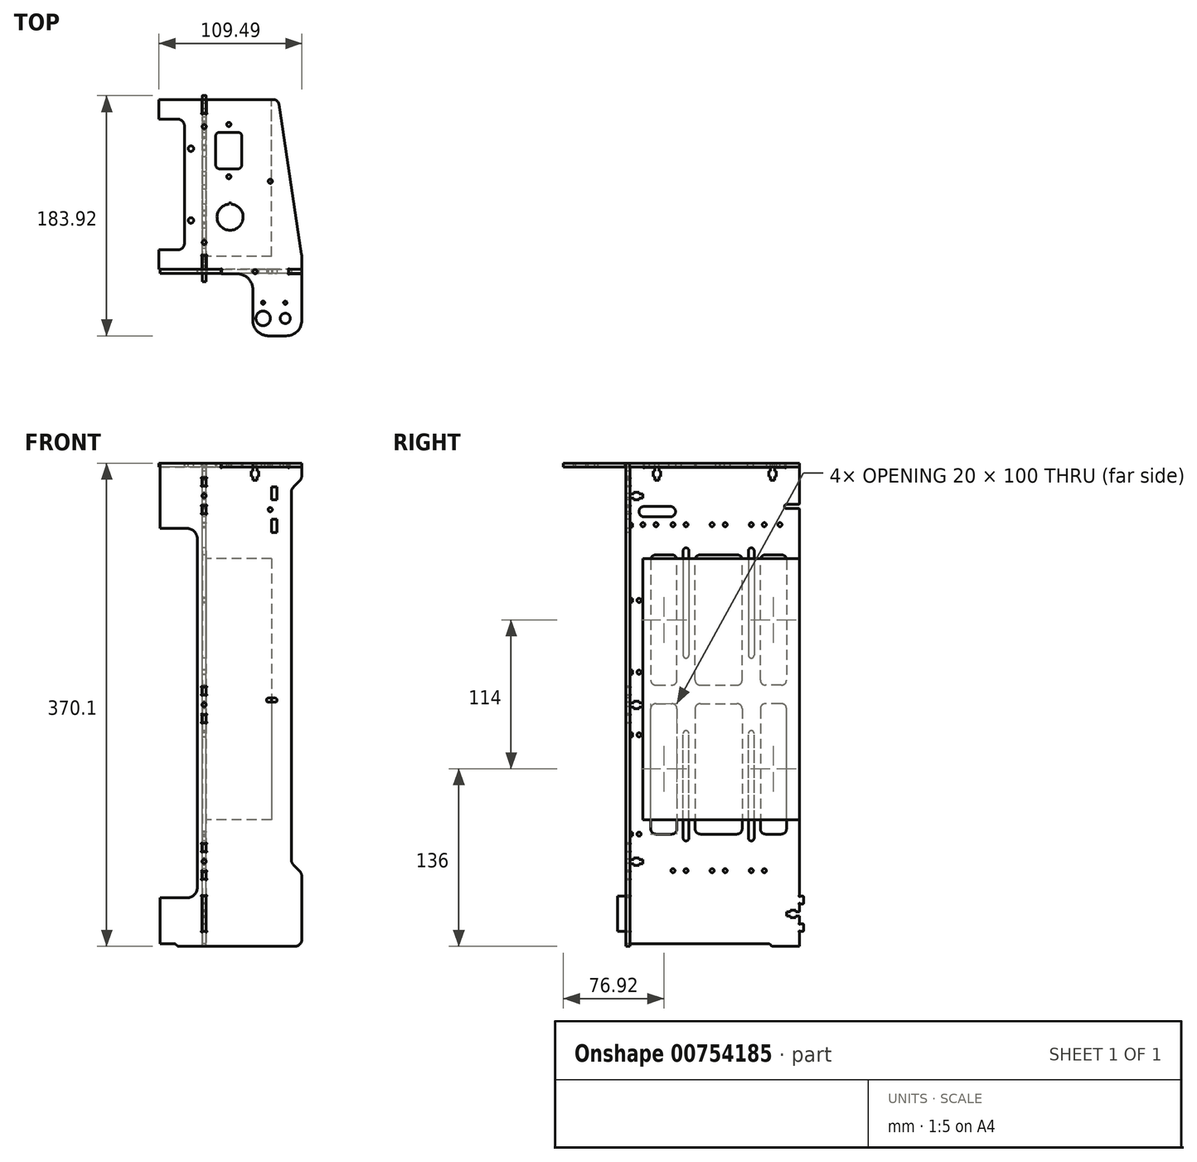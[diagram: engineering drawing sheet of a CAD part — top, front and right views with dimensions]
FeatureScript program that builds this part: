
annotation { "Feature Type Name" : "Feature", "Feature Type Description" : "" }
export const myFeature = defineFeature(function(context is Context, id is Id, definition is map)
    precondition{}
    {
        {
            assignVariable(context, id + "F0", {"name" : "profondeur_alim", "anyValue" : 50});
        }
        {
            var Q0;
            Q0=qCreatedBy(makeId("Top.planeOp"),FACE);
            var sketch = newSketch(context, id + "F1", { "sketchPlane" : qUnion([Q0])});
            skLineSegment(sketch, "E0", {"start": v(194.9, -37.1) * mm, "end": v(185.77, -37.1) * mm});
            skArc(sketch, "E1", {"start": v(185.33, -36.84) * mm, "mid": v(185.52, -37.03) * mm, "end": v(185.77, -37.1) * mm});
            skArc(sketch, "E2", {"start": v(185.33, -36.84) * mm, "mid": v(184.55, -36.74) * mm, "end": v(184.65, -37.53) * mm});
            skArc(sketch, "E3", {"start": v(184.9, -37.96) * mm, "mid": v(184.83, -37.71) * mm, "end": v(184.65, -37.53) * mm});
            skLineSegment(sketch, "E4", {"start": v(184.9, -37.96) * mm, "end": v(184.9, -39.53) * mm});
            skArc(sketch, "E5", {"start": v(184.65, -39.96) * mm, "mid": v(184.83, -39.78) * mm, "end": v(184.9, -39.53) * mm});
            skArc(sketch, "E6", {"start": v(184.65, -39.96) * mm, "mid": v(184.55, -40.75) * mm, "end": v(185.33, -40.64) * mm});
            skArc(sketch, "E7", {"start": v(185.77, -40.4) * mm, "mid": v(185.52, -40.46) * mm, "end": v(185.33, -40.64) * mm});
            skLineSegment(sketch, "E8", {"start": v(185.77, -40.4) * mm, "end": v(194.9, -40.4) * mm});
            skCircle(sketch, "E9", {"center": v(159.08, -38.74) * mm, "radius": 1.6 * mm});
            skLineSegment(sketch, "E10", {"start": v(133.25, -40.4) * mm, "end": v(133.25, -37.92) * mm});
            skArc(sketch, "E11", {"start": v(133.5, -37.48) * mm, "mid": v(133.32, -37.67) * mm, "end": v(133.25, -37.92) * mm});
            skArc(sketch, "E12", {"start": v(133.5, -37.48) * mm, "mid": v(133.6, -36.7) * mm, "end": v(132.82, -36.8) * mm});
            skArc(sketch, "E13", {"start": v(132.38, -37.05) * mm, "mid": v(132.63, -36.98) * mm, "end": v(132.82, -36.8) * mm});
            skLineSegment(sketch, "E14", {"start": v(132.38, -37.05) * mm, "end": v(121.73, -37.05) * mm});
            skLineSegment(sketch, "E15", {"start": v(121.73, -37.05) * mm, "end": v(121.73, -27.27) * mm});
            skArc(sketch, "E16", {"start": v(121.98, -26.83) * mm, "mid": v(121.8, -27.02) * mm, "end": v(121.73, -27.27) * mm});
            skArc(sketch, "E17", {"start": v(121.98, -26.83) * mm, "mid": v(122.08, -26.05) * mm, "end": v(121.3, -26.15) * mm});
            skArc(sketch, "E18", {"start": v(120.86, -26.4) * mm, "mid": v(121.1, -26.33) * mm, "end": v(121.3, -26.15) * mm});
            skLineSegment(sketch, "E19", {"start": v(120.86, -26.4) * mm, "end": v(119.3, -26.4) * mm});
            skArc(sketch, "E20", {"start": v(118.86, -26.15) * mm, "mid": v(119.04, -26.33) * mm, "end": v(119.3, -26.4) * mm});
            skArc(sketch, "E21", {"start": v(118.86, -26.15) * mm, "mid": v(118.07, -26.05) * mm, "end": v(118.18, -26.83) * mm});
            skArc(sketch, "E22", {"start": v(118.43, -27.27) * mm, "mid": v(118.36, -27.02) * mm, "end": v(118.18, -26.83) * mm});
            skLineSegment(sketch, "E23", {"start": v(118.43, -27.27) * mm, "end": v(118.43, -37.05) * mm});
            skCircle(sketch, "E24", {"center": v(120.08, -16.4) * mm, "radius": 1.6 * mm});
            skLineSegment(sketch, "E25", {"start": v(118.43, -37.05) * mm, "end": v(85.41, -37.05) * mm});
            skArc(sketch, "E26", {"start": v(99.9, -22.05) * mm, "mid": v(103.44, -20.58) * mm, "end": v(104.9, -17.05) * mm});
            skLineSegment(sketch, "E27", {"start": v(99.9, -22.05) * mm, "end": v(85.41, -22.05) * mm});
            skCircle(sketch, "E28", {"center": v(109.9, 0.45) * mm, "radius": 2.1 * mm});
            skLineSegment(sketch, "E29", {"start": v(194.9, -40.4) * mm, "end": v(194.9, -75.92) * mm});
            skArc(sketch, "E30", {"start": v(182.9, -87.92) * mm, "mid": v(191.39, -84.4) * mm, "end": v(194.9, -75.92) * mm});
            skCircle(sketch, "E31", {"center": v(182.2, -62.54) * mm, "radius": 1.25 * mm});
            skCircle(sketch, "E32", {"center": v(165.2, -74.55) * mm, "radius": 5.53 * mm});
            skCircle(sketch, "E33", {"center": v(165.2, -62.54) * mm, "radius": 1.25 * mm});
            skCircle(sketch, "E34", {"center": v(182.2, -74.54) * mm, "radius": 3.9 * mm});
            skLineSegment(sketch, "E35", {"start": v(194.9, -37.1) * mm, "end": v(194.9, -28.66) * mm});
            skArc(sketch, "E36", {"start": v(194.9, -28.66) * mm, "mid": v(194.84, -27.1) * mm, "end": v(194.66, -25.54) * mm});
            skCircle(sketch, "E37", {"center": v(120.08, 72.3) * mm, "radius": 1.6 * mm});
            skArc(sketch, "E38", {"start": v(104.9, 72.95) * mm, "mid": v(103.44, 76.49) * mm, "end": v(99.9, 77.95) * mm});
            skLineSegment(sketch, "E39", {"start": v(85.41, 77.95) * mm, "end": v(99.9, 77.95) * mm});
            skLineSegment(sketch, "E40", {"start": v(104.9, 72.95) * mm, "end": v(104.9, -17.05) * mm});
            skLineSegment(sketch, "E41", {"start": v(121.72, 92.95) * mm, "end": v(121.72, 83.17) * mm});
            skArc(sketch, "E42", {"start": v(121.72, 83.17) * mm, "mid": v(121.8, 82.92) * mm, "end": v(121.97, 82.73) * mm});
            skArc(sketch, "E43", {"start": v(121.3, 82.05) * mm, "mid": v(122.08, 81.95) * mm, "end": v(121.97, 82.73) * mm});
            skArc(sketch, "E44", {"start": v(121.3, 82.05) * mm, "mid": v(121.1, 82.23) * mm, "end": v(120.86, 82.3) * mm});
            skLineSegment(sketch, "E45", {"start": v(120.86, 82.3) * mm, "end": v(119.3, 82.3) * mm});
            skArc(sketch, "E46", {"start": v(119.3, 82.3) * mm, "mid": v(119.04, 82.23) * mm, "end": v(118.86, 82.05) * mm});
            skArc(sketch, "E47", {"start": v(118.17, 82.74) * mm, "mid": v(118.07, 81.95) * mm, "end": v(118.86, 82.05) * mm});
            skArc(sketch, "E48", {"start": v(118.17, 82.74) * mm, "mid": v(118.36, 82.92) * mm, "end": v(118.42, 83.17) * mm});
            skLineSegment(sketch, "E49", {"start": v(118.42, 83.17) * mm, "end": v(118.42, 92.95) * mm});
            skLineSegment(sketch, "E50", {"start": v(118.42, 92.95) * mm, "end": v(85.41, 92.95) * mm});
            skLineSegment(sketch, "E51", {"start": v(173.3, 92.95) * mm, "end": v(121.72, 92.95) * mm});
            skArc(sketch, "E52", {"start": v(177.26, 89.57) * mm, "mid": v(175.9, 92) * mm, "end": v(173.3, 92.95) * mm});
            skLineSegment(sketch, "E53", {"start": v(194.66, -25.54) * mm, "end": v(177.26, 89.57) * mm});
            skCircle(sketch, "E54", {"center": v(109.9, 55.45) * mm, "radius": 2.1 * mm});
            skArc(sketch, "E55", {"start": v(157.3, -52.4) * mm, "mid": v(153.78, -43.91) * mm, "end": v(145.29, -40.4) * mm});
            skArc(sketch, "E56", {"start": v(157.3, -75.92) * mm, "mid": v(160.8, -84.4) * mm, "end": v(169.3, -87.92) * mm});
            skLineSegment(sketch, "E57", {"start": v(157.3, -52.4) * mm, "end": v(157.3, -75.92) * mm});
            skLineSegment(sketch, "E58", {"start": v(145.29, -40.4) * mm, "end": v(133.25, -40.4) * mm});
            skLineSegment(sketch, "E59", {"start": v(169.3, -87.92) * mm, "end": v(182.9, -87.92) * mm});
            skCircle(sketch, "E60", {"center": v(138.87, 33.99) * mm, "radius": 1.6 * mm});
            skArc(sketch, "E61", {"start": v(145.87, 39.99) * mm, "mid": v(148, 40.87) * mm, "end": v(148.87, 42.99) * mm});
            skLineSegment(sketch, "E62", {"start": v(145.87, 39.99) * mm, "end": v(131.87, 39.99) * mm});
            skArc(sketch, "E63", {"start": v(128.87, 42.99) * mm, "mid": v(129.75, 40.87) * mm, "end": v(131.87, 39.99) * mm});
            skLineSegment(sketch, "E64", {"start": v(128.87, 64.99) * mm, "end": v(128.87, 42.99) * mm});
            skArc(sketch, "E65", {"start": v(131.87, 67.99) * mm, "mid": v(129.75, 67.1) * mm, "end": v(128.87, 64.99) * mm});
            skLineSegment(sketch, "E66", {"start": v(145.87, 67.99) * mm, "end": v(131.87, 67.99) * mm});
            skArc(sketch, "E67", {"start": v(148.87, 64.99) * mm, "mid": v(148, 67.1) * mm, "end": v(145.87, 67.99) * mm});
            skLineSegment(sketch, "E68", {"start": v(148.87, 64.99) * mm, "end": v(148.87, 42.99) * mm});
            skCircle(sketch, "E69", {"center": v(138.87, 73.99) * mm, "radius": 1.6 * mm});
            skArc(sketch, "E70", {"start": v(138.8, 12.89) * mm, "mid": v(139.9, -7.05) * mm, "end": v(141, 12.89) * mm});
            skLineSegment(sketch, "E71", {"start": v(141, 13.95) * mm, "end": v(141, 12.9) * mm});
            skLineSegment(sketch, "E72", {"start": v(138.8, 13.95) * mm, "end": v(138.8, 12.9) * mm});
            skLineSegment(sketch, "E73", {"start": v(138.8, 13.95) * mm, "end": v(141, 13.95) * mm});
            skCircle(sketch, "E74", {"center": v(170.72, 30.45) * mm, "radius": 1.6 * mm});
            skLineSegment(sketch, "E75", {"start": v(85.41, -37.05) * mm, "end": v(85.41, -22.05) * mm});
            skLineSegment(sketch, "E76", {"start": v(76.17, 13.3) * mm, "end": v(24.44, 13.3) * mm, "construction": true});
            skPoint(sketch, "E77.end.orphan", {"position": v(52.4, -36.45) * mm});
            skLineSegment(sketch, "E78.trimOffspring", {"start": v(85.41, 77.95) * mm, "end": v(85.41, 92.95) * mm});
            skSolve(sketch);
        }
        {
            var Q0;
            Q0=makeQuery(id+"F1.imprint","IMPRINT",FACE,{"disambiguationData":[TD([[makeQuery(id+"F1.imprint","IMPRINT",EDGE,{"derivedFrom":sQuery(id+"F1.wireOp",EDGE,"E0")}),-1.0]])]});
            extrude(context, id + "F2", {"entities" : qUnion([Q0]), "oppositeDirection" : true, "depth" : 3 * mm, "offsetDistance" : 25 * mm});
        }
        {
            var Q0;
            Q0=qCreatedBy(makeId("Front.planeOp"),FACE);
            cPlane(context, id + "F3", {"entities" : qUnion([Q0]), "cplaneType" : CPlaneType.OFFSET, "offset" : 40 * mm, "width" : 150 * mm, "height" : 150 * mm});
        }
        {
            var Q0;
            Q0=qCreatedBy(id+"F3.planeOp",FACE);
            var sketch = newSketch(context, id + "F4", { "sketchPlane" : qUnion([Q0])});
            skArc(sketch, "E79", {"start": v(189.8, -369.9) * mm, "mid": v(193.34, -368.44) * mm, "end": v(194.8, -364.9) * mm});
            skLineSegment(sketch, "E80", {"start": v(194.8, 0.1) * mm, "end": v(184.8, 0.1) * mm});
            skLineSegment(sketch, "E81", {"start": v(184.8, 0.1) * mm, "end": v(184.8, -2.13) * mm});
            skArc(sketch, "E82", {"start": v(184.8, -2.13) * mm, "mid": v(184.87, -2.38) * mm, "end": v(185.06, -2.57) * mm});
            skArc(sketch, "E83", {"start": v(184.37, -3.25) * mm, "mid": v(185.16, -3.35) * mm, "end": v(185.06, -2.57) * mm});
            skArc(sketch, "E84", {"start": v(184.37, -3.25) * mm, "mid": v(184.19, -3.07) * mm, "end": v(183.94, -3) * mm});
            skLineSegment(sketch, "E85", {"start": v(183.94, -3) * mm, "end": v(160.58, -3) * mm});
            skLineSegment(sketch, "E86", {"start": v(160.58, -3) * mm, "end": v(160.58, -6) * mm});
            skLineSegment(sketch, "E87", {"start": v(160.58, -6) * mm, "end": v(161.86, -6) * mm});
            skLineSegment(sketch, "E88", {"start": v(161.86, -6) * mm, "end": v(161.86, -10) * mm});
            skLineSegment(sketch, "E89", {"start": v(161.86, -10) * mm, "end": v(160.58, -10) * mm});
            skLineSegment(sketch, "E90", {"start": v(160.58, -10) * mm, "end": v(160.58, -13) * mm});
            skLineSegment(sketch, "E91", {"start": v(160.58, -13) * mm, "end": v(157.38, -13) * mm});
            skLineSegment(sketch, "E92", {"start": v(157.38, -13) * mm, "end": v(157.38, -10) * mm});
            skLineSegment(sketch, "E93", {"start": v(157.38, -10) * mm, "end": v(156.1, -10) * mm});
            skLineSegment(sketch, "E94", {"start": v(156.1, -10) * mm, "end": v(156.1, -6) * mm});
            skLineSegment(sketch, "E95", {"start": v(156.1, -6) * mm, "end": v(157.38, -6) * mm});
            skLineSegment(sketch, "E96", {"start": v(157.38, -6) * mm, "end": v(157.38, -3) * mm});
            skLineSegment(sketch, "E97", {"start": v(106.8, -49.9) * mm, "end": v(86.12, -49.9) * mm});
            skArc(sketch, "E98", {"start": v(120.76, -331.2) * mm, "mid": v(121.01, -331.13) * mm, "end": v(121.2, -330.95) * mm});
            skArc(sketch, "E99", {"start": v(121.88, -331.63) * mm, "mid": v(121.98, -330.85) * mm, "end": v(121.2, -330.95) * mm});
            skArc(sketch, "E100", {"start": v(121.88, -331.63) * mm, "mid": v(121.7, -331.82) * mm, "end": v(121.63, -332.07) * mm});
            skLineSegment(sketch, "E101", {"start": v(121.63, -332.07) * mm, "end": v(121.63, -357.73) * mm});
            skArc(sketch, "E102", {"start": v(121.63, -357.73) * mm, "mid": v(121.7, -357.98) * mm, "end": v(121.88, -358.17) * mm});
            skArc(sketch, "E103", {"start": v(121.2, -358.85) * mm, "mid": v(121.98, -358.95) * mm, "end": v(121.88, -358.17) * mm});
            skArc(sketch, "E104", {"start": v(121.2, -358.85) * mm, "mid": v(121.01, -358.67) * mm, "end": v(120.76, -358.6) * mm});
            skLineSegment(sketch, "E105", {"start": v(120.76, -358.6) * mm, "end": v(119.2, -358.6) * mm});
            skArc(sketch, "E106", {"start": v(119.2, -358.6) * mm, "mid": v(118.95, -358.67) * mm, "end": v(118.76, -358.85) * mm});
            skArc(sketch, "E107", {"start": v(118.08, -358.17) * mm, "mid": v(117.98, -358.95) * mm, "end": v(118.76, -358.85) * mm});
            skArc(sketch, "E108", {"start": v(118.08, -358.17) * mm, "mid": v(118.26, -357.98) * mm, "end": v(118.33, -357.73) * mm});
            skLineSegment(sketch, "E109", {"start": v(118.33, -357.73) * mm, "end": v(118.33, -332.07) * mm});
            skArc(sketch, "E110", {"start": v(118.33, -332.07) * mm, "mid": v(118.26, -331.82) * mm, "end": v(118.08, -331.63) * mm});
            skArc(sketch, "E111", {"start": v(118.76, -330.95) * mm, "mid": v(117.98, -330.85) * mm, "end": v(118.08, -331.63) * mm});
            skArc(sketch, "E112", {"start": v(118.76, -330.95) * mm, "mid": v(118.95, -331.13) * mm, "end": v(119.2, -331.2) * mm});
            skLineSegment(sketch, "E113", {"start": v(119.2, -331.2) * mm, "end": v(120.76, -331.2) * mm});
            skArc(sketch, "E114", {"start": v(118.76, -312.15) * mm, "mid": v(118.95, -312.33) * mm, "end": v(119.2, -312.4) * mm});
            skArc(sketch, "E115", {"start": v(118.76, -312.15) * mm, "mid": v(117.98, -312.05) * mm, "end": v(118.08, -312.83) * mm});
            skArc(sketch, "E116", {"start": v(118.33, -313.27) * mm, "mid": v(118.26, -313.02) * mm, "end": v(118.08, -312.83) * mm});
            skLineSegment(sketch, "E117", {"start": v(118.33, -313.27) * mm, "end": v(118.33, -317.73) * mm});
            skArc(sketch, "E118", {"start": v(118.08, -318.17) * mm, "mid": v(118.26, -317.98) * mm, "end": v(118.33, -317.73) * mm});
            skArc(sketch, "E119", {"start": v(118.08, -318.17) * mm, "mid": v(117.98, -318.95) * mm, "end": v(118.76, -318.85) * mm});
            skArc(sketch, "E120", {"start": v(119.2, -318.6) * mm, "mid": v(118.95, -318.67) * mm, "end": v(118.76, -318.85) * mm});
            skLineSegment(sketch, "E121", {"start": v(119.2, -318.6) * mm, "end": v(120.76, -318.6) * mm});
            skArc(sketch, "E122", {"start": v(121.2, -318.85) * mm, "mid": v(121.01, -318.67) * mm, "end": v(120.76, -318.6) * mm});
            skArc(sketch, "E123", {"start": v(121.2, -318.85) * mm, "mid": v(121.98, -318.95) * mm, "end": v(121.88, -318.17) * mm});
            skArc(sketch, "E124", {"start": v(121.63, -317.73) * mm, "mid": v(121.7, -317.98) * mm, "end": v(121.88, -318.17) * mm});
            skLineSegment(sketch, "E125", {"start": v(121.63, -317.73) * mm, "end": v(121.63, -313.27) * mm});
            skArc(sketch, "E126", {"start": v(121.88, -312.83) * mm, "mid": v(121.7, -313.02) * mm, "end": v(121.63, -313.27) * mm});
            skArc(sketch, "E127", {"start": v(121.88, -312.83) * mm, "mid": v(121.98, -312.05) * mm, "end": v(121.2, -312.15) * mm});
            skArc(sketch, "E128", {"start": v(120.76, -312.4) * mm, "mid": v(121.01, -312.33) * mm, "end": v(121.2, -312.15) * mm});
            skLineSegment(sketch, "E129", {"start": v(120.76, -312.4) * mm, "end": v(119.2, -312.4) * mm});
            skArc(sketch, "E130", {"start": v(118.76, -290.95) * mm, "mid": v(118.95, -291.13) * mm, "end": v(119.2, -291.2) * mm});
            skArc(sketch, "E131", {"start": v(118.76, -290.95) * mm, "mid": v(117.98, -290.85) * mm, "end": v(118.08, -291.63) * mm});
            skArc(sketch, "E132", {"start": v(118.33, -292.07) * mm, "mid": v(118.26, -291.82) * mm, "end": v(118.08, -291.63) * mm});
            skLineSegment(sketch, "E133", {"start": v(118.33, -292.07) * mm, "end": v(118.33, -296.53) * mm});
            skArc(sketch, "E134", {"start": v(118.08, -296.97) * mm, "mid": v(118.26, -296.78) * mm, "end": v(118.33, -296.53) * mm});
            skArc(sketch, "E135", {"start": v(118.08, -296.97) * mm, "mid": v(117.98, -297.75) * mm, "end": v(118.76, -297.65) * mm});
            skArc(sketch, "E136", {"start": v(119.2, -297.4) * mm, "mid": v(118.95, -297.47) * mm, "end": v(118.76, -297.65) * mm});
            skLineSegment(sketch, "E137", {"start": v(119.2, -297.4) * mm, "end": v(120.76, -297.4) * mm});
            skArc(sketch, "E138", {"start": v(121.2, -297.65) * mm, "mid": v(121.01, -297.47) * mm, "end": v(120.76, -297.4) * mm});
            skArc(sketch, "E139", {"start": v(121.2, -297.65) * mm, "mid": v(121.98, -297.75) * mm, "end": v(121.88, -296.97) * mm});
            skArc(sketch, "E140", {"start": v(121.63, -296.53) * mm, "mid": v(121.7, -296.78) * mm, "end": v(121.88, -296.97) * mm});
            skLineSegment(sketch, "E141", {"start": v(121.63, -296.53) * mm, "end": v(121.63, -292.07) * mm});
            skArc(sketch, "E142", {"start": v(121.88, -291.63) * mm, "mid": v(121.7, -291.82) * mm, "end": v(121.63, -292.07) * mm});
            skArc(sketch, "E143", {"start": v(121.88, -291.63) * mm, "mid": v(121.98, -290.85) * mm, "end": v(121.2, -290.95) * mm});
            skArc(sketch, "E144", {"start": v(120.76, -291.2) * mm, "mid": v(121.01, -291.13) * mm, "end": v(121.2, -290.95) * mm});
            skLineSegment(sketch, "E145", {"start": v(120.76, -291.2) * mm, "end": v(119.2, -291.2) * mm});
            skArc(sketch, "E146", {"start": v(120.76, -192.4) * mm, "mid": v(121.01, -192.33) * mm, "end": v(121.2, -192.15) * mm});
            skArc(sketch, "E147", {"start": v(121.88, -192.83) * mm, "mid": v(121.98, -192.05) * mm, "end": v(121.2, -192.15) * mm});
            skArc(sketch, "E148", {"start": v(121.88, -192.83) * mm, "mid": v(121.7, -193.02) * mm, "end": v(121.63, -193.27) * mm});
            skLineSegment(sketch, "E149", {"start": v(121.63, -193.27) * mm, "end": v(121.63, -197.73) * mm});
            skArc(sketch, "E150", {"start": v(121.63, -197.73) * mm, "mid": v(121.7, -197.98) * mm, "end": v(121.88, -198.17) * mm});
            skArc(sketch, "E151", {"start": v(121.2, -198.85) * mm, "mid": v(121.98, -198.95) * mm, "end": v(121.88, -198.17) * mm});
            skArc(sketch, "E152", {"start": v(121.2, -198.85) * mm, "mid": v(121.01, -198.67) * mm, "end": v(120.76, -198.6) * mm});
            skLineSegment(sketch, "E153", {"start": v(120.76, -198.6) * mm, "end": v(119.2, -198.6) * mm});
            skArc(sketch, "E154", {"start": v(119.2, -198.6) * mm, "mid": v(118.95, -198.67) * mm, "end": v(118.76, -198.85) * mm});
            skArc(sketch, "E155", {"start": v(118.08, -198.17) * mm, "mid": v(117.98, -198.95) * mm, "end": v(118.76, -198.85) * mm});
            skArc(sketch, "E156", {"start": v(118.08, -198.17) * mm, "mid": v(118.26, -197.98) * mm, "end": v(118.33, -197.73) * mm});
            skLineSegment(sketch, "E157", {"start": v(118.33, -197.73) * mm, "end": v(118.33, -193.27) * mm});
            skArc(sketch, "E158", {"start": v(118.33, -193.27) * mm, "mid": v(118.26, -193.02) * mm, "end": v(118.08, -192.83) * mm});
            skArc(sketch, "E159", {"start": v(118.76, -192.15) * mm, "mid": v(117.98, -192.05) * mm, "end": v(118.08, -192.83) * mm});
            skArc(sketch, "E160", {"start": v(118.76, -192.15) * mm, "mid": v(118.95, -192.33) * mm, "end": v(119.2, -192.4) * mm});
            skLineSegment(sketch, "E161", {"start": v(119.2, -192.4) * mm, "end": v(120.76, -192.4) * mm});
            skArc(sketch, "E162", {"start": v(120.76, -171.2) * mm, "mid": v(121.01, -171.13) * mm, "end": v(121.2, -170.95) * mm});
            skArc(sketch, "E163", {"start": v(121.88, -171.63) * mm, "mid": v(121.98, -170.85) * mm, "end": v(121.2, -170.95) * mm});
            skArc(sketch, "E164", {"start": v(121.88, -171.63) * mm, "mid": v(121.7, -171.82) * mm, "end": v(121.63, -172.07) * mm});
            skLineSegment(sketch, "E165", {"start": v(121.63, -172.07) * mm, "end": v(121.63, -176.53) * mm});
            skArc(sketch, "E166", {"start": v(121.63, -176.53) * mm, "mid": v(121.7, -176.78) * mm, "end": v(121.88, -176.97) * mm});
            skArc(sketch, "E167", {"start": v(121.2, -177.65) * mm, "mid": v(121.98, -177.75) * mm, "end": v(121.88, -176.97) * mm});
            skArc(sketch, "E168", {"start": v(121.2, -177.65) * mm, "mid": v(121.01, -177.47) * mm, "end": v(120.76, -177.4) * mm});
            skLineSegment(sketch, "E169", {"start": v(120.76, -177.4) * mm, "end": v(119.2, -177.4) * mm});
            skArc(sketch, "E170", {"start": v(119.2, -177.4) * mm, "mid": v(118.95, -177.47) * mm, "end": v(118.76, -177.65) * mm});
            skArc(sketch, "E171", {"start": v(118.08, -176.97) * mm, "mid": v(117.98, -177.75) * mm, "end": v(118.76, -177.65) * mm});
            skArc(sketch, "E172", {"start": v(118.08, -176.97) * mm, "mid": v(118.26, -176.78) * mm, "end": v(118.33, -176.53) * mm});
            skLineSegment(sketch, "E173", {"start": v(118.33, -176.53) * mm, "end": v(118.33, -172.07) * mm});
            skArc(sketch, "E174", {"start": v(118.33, -172.07) * mm, "mid": v(118.26, -171.82) * mm, "end": v(118.08, -171.63) * mm});
            skArc(sketch, "E175", {"start": v(118.76, -170.95) * mm, "mid": v(117.98, -170.85) * mm, "end": v(118.08, -171.63) * mm});
            skArc(sketch, "E176", {"start": v(118.76, -170.95) * mm, "mid": v(118.95, -171.13) * mm, "end": v(119.2, -171.2) * mm});
            skLineSegment(sketch, "E177", {"start": v(119.2, -171.2) * mm, "end": v(120.76, -171.2) * mm});
            skArc(sketch, "E178", {"start": v(120.76, -32.4) * mm, "mid": v(121.01, -32.33) * mm, "end": v(121.2, -32.15) * mm});
            skArc(sketch, "E179", {"start": v(121.88, -32.83) * mm, "mid": v(121.98, -32.05) * mm, "end": v(121.2, -32.15) * mm});
            skArc(sketch, "E180", {"start": v(121.88, -32.83) * mm, "mid": v(121.7, -33.02) * mm, "end": v(121.63, -33.27) * mm});
            skLineSegment(sketch, "E181", {"start": v(121.63, -33.27) * mm, "end": v(121.63, -37.73) * mm});
            skArc(sketch, "E182", {"start": v(121.63, -37.73) * mm, "mid": v(121.7, -37.98) * mm, "end": v(121.88, -38.17) * mm});
            skArc(sketch, "E183", {"start": v(121.2, -38.85) * mm, "mid": v(121.98, -38.95) * mm, "end": v(121.88, -38.17) * mm});
            skArc(sketch, "E184", {"start": v(121.2, -38.85) * mm, "mid": v(121.01, -38.67) * mm, "end": v(120.76, -38.6) * mm});
            skLineSegment(sketch, "E185", {"start": v(120.76, -38.6) * mm, "end": v(119.2, -38.6) * mm});
            skArc(sketch, "E186", {"start": v(119.2, -38.6) * mm, "mid": v(118.95, -38.67) * mm, "end": v(118.76, -38.85) * mm});
            skArc(sketch, "E187", {"start": v(118.08, -38.17) * mm, "mid": v(117.98, -38.95) * mm, "end": v(118.76, -38.85) * mm});
            skArc(sketch, "E188", {"start": v(118.08, -38.17) * mm, "mid": v(118.26, -37.98) * mm, "end": v(118.33, -37.73) * mm});
            skLineSegment(sketch, "E189", {"start": v(118.33, -37.73) * mm, "end": v(118.33, -33.27) * mm});
            skArc(sketch, "E190", {"start": v(118.33, -33.27) * mm, "mid": v(118.26, -33.02) * mm, "end": v(118.08, -32.83) * mm});
            skArc(sketch, "E191", {"start": v(118.76, -32.15) * mm, "mid": v(117.98, -32.05) * mm, "end": v(118.08, -32.83) * mm});
            skArc(sketch, "E192", {"start": v(118.76, -32.15) * mm, "mid": v(118.95, -32.33) * mm, "end": v(119.2, -32.4) * mm});
            skLineSegment(sketch, "E193", {"start": v(119.2, -32.4) * mm, "end": v(120.76, -32.4) * mm});
            skArc(sketch, "E194", {"start": v(120.76, -11.2) * mm, "mid": v(121.01, -11.13) * mm, "end": v(121.2, -10.95) * mm});
            skArc(sketch, "E195", {"start": v(121.88, -11.63) * mm, "mid": v(121.98, -10.85) * mm, "end": v(121.2, -10.95) * mm});
            skArc(sketch, "E196", {"start": v(121.88, -11.63) * mm, "mid": v(121.7, -11.82) * mm, "end": v(121.63, -12.07) * mm});
            skLineSegment(sketch, "E197", {"start": v(121.63, -12.07) * mm, "end": v(121.63, -16.53) * mm});
            skArc(sketch, "E198", {"start": v(121.63, -16.53) * mm, "mid": v(121.7, -16.78) * mm, "end": v(121.88, -16.97) * mm});
            skArc(sketch, "E199", {"start": v(121.2, -17.65) * mm, "mid": v(121.98, -17.75) * mm, "end": v(121.88, -16.97) * mm});
            skArc(sketch, "E200", {"start": v(121.2, -17.65) * mm, "mid": v(121.01, -17.47) * mm, "end": v(120.76, -17.4) * mm});
            skLineSegment(sketch, "E201", {"start": v(120.76, -17.4) * mm, "end": v(119.2, -17.4) * mm});
            skArc(sketch, "E202", {"start": v(119.2, -17.4) * mm, "mid": v(118.95, -17.47) * mm, "end": v(118.76, -17.65) * mm});
            skArc(sketch, "E203", {"start": v(118.08, -16.97) * mm, "mid": v(117.98, -17.75) * mm, "end": v(118.76, -17.65) * mm});
            skArc(sketch, "E204", {"start": v(118.08, -16.97) * mm, "mid": v(118.26, -16.78) * mm, "end": v(118.33, -16.53) * mm});
            skLineSegment(sketch, "E205", {"start": v(118.33, -16.53) * mm, "end": v(118.33, -12.07) * mm});
            skArc(sketch, "E206", {"start": v(118.33, -12.07) * mm, "mid": v(118.26, -11.82) * mm, "end": v(118.08, -11.63) * mm});
            skArc(sketch, "E207", {"start": v(118.76, -10.95) * mm, "mid": v(117.98, -10.85) * mm, "end": v(118.08, -11.63) * mm});
            skArc(sketch, "E208", {"start": v(118.76, -10.95) * mm, "mid": v(118.95, -11.13) * mm, "end": v(119.2, -11.2) * mm});
            skLineSegment(sketch, "E209", {"start": v(119.2, -11.2) * mm, "end": v(120.76, -11.2) * mm});
            skCircle(sketch, "E210", {"center": v(119.98, -304.9) * mm, "radius": 1.6 * mm});
            skCircle(sketch, "E211", {"center": v(119.98, -184.9) * mm, "radius": 1.6 * mm});
            skCircle(sketch, "E212", {"center": v(119.98, -24.9) * mm, "radius": 1.6 * mm});
            skLineSegment(sketch, "E213", {"start": v(114.8, -324.8) * mm, "end": v(114.8, -57.9) * mm});
            skArc(sketch, "E214", {"start": v(106.8, -332.78) * mm, "mid": v(112.46, -330.44) * mm, "end": v(114.8, -324.8) * mm});
            skLineSegment(sketch, "E215", {"start": v(133, 0.1) * mm, "end": v(86.12, 0.1) * mm});
            skArc(sketch, "E216", {"start": v(133.87, -3) * mm, "mid": v(133.62, -3.07) * mm, "end": v(133.44, -3.25) * mm});
            skArc(sketch, "E217", {"start": v(132.76, -2.57) * mm, "mid": v(132.65, -3.35) * mm, "end": v(133.44, -3.25) * mm});
            skArc(sketch, "E218", {"start": v(132.76, -2.57) * mm, "mid": v(132.94, -2.38) * mm, "end": v(133, -2.13) * mm});
            skLineSegment(sketch, "E219", {"start": v(133, -2.13) * mm, "end": v(133, 0.1) * mm});
            skLineSegment(sketch, "E220", {"start": v(157.38, -3) * mm, "end": v(133.87, -3) * mm});
            skLineSegment(sketch, "E221", {"start": v(194.8, -364.9) * mm, "end": v(194.8, -316.36) * mm});
            skArc(sketch, "E222", {"start": v(194.8, -316.36) * mm, "mid": v(194.36, -314.09) * mm, "end": v(193.07, -312.15) * mm});
            skLineSegment(sketch, "E223", {"start": v(188.54, -307.56) * mm, "end": v(193.07, -312.15) * mm});
            skArc(sketch, "E224", {"start": v(186.8, -303.34) * mm, "mid": v(187.26, -305.62) * mm, "end": v(188.54, -307.56) * mm});
            skLineSegment(sketch, "E225", {"start": v(194.8, -9.42) * mm, "end": v(194.8, 0.1) * mm});
            skArc(sketch, "E226", {"start": v(193.05, -13.66) * mm, "mid": v(194.35, -11.71) * mm, "end": v(194.8, -9.42) * mm});
            skLineSegment(sketch, "E227", {"start": v(193.05, -13.66) * mm, "end": v(188.56, -18.14) * mm});
            skArc(sketch, "E228", {"start": v(188.56, -18.14) * mm, "mid": v(187.26, -20.09) * mm, "end": v(186.8, -22.39) * mm});
            skLineSegment(sketch, "E229", {"start": v(106.8, -332.78) * mm, "end": v(86.12, -332.78) * mm});
            skArc(sketch, "E230", {"start": v(98.1, -368.2) * mm, "mid": v(97.77, -367.98) * mm, "end": v(97.4, -367.9) * mm});
            skLineSegment(sketch, "E231", {"start": v(189.8, -369.9) * mm, "end": v(100.22, -369.9) * mm});
            skLineSegment(sketch, "E232", {"start": v(98.1, -368.2) * mm, "end": v(99.51, -369.6) * mm});
            skArc(sketch, "E233", {"start": v(99.51, -369.6) * mm, "mid": v(99.84, -369.82) * mm, "end": v(100.22, -369.9) * mm});
            skArc(sketch, "E234", {"start": v(174.3, -183) * mm, "mid": v(175.9, -181.4) * mm, "end": v(174.3, -179.8) * mm});
            skArc(sketch, "E235", {"start": v(169.3, -179.8) * mm, "mid": v(167.7, -181.4) * mm, "end": v(169.3, -183) * mm});
            skLineSegment(sketch, "E236", {"start": v(174.3, -179.8) * mm, "end": v(169.3, -179.8) * mm});
            skLineSegment(sketch, "E237", {"start": v(174.3, -183) * mm, "end": v(169.3, -183) * mm});
            skLineSegment(sketch, "E238", {"start": v(186.8, -22.39) * mm, "end": v(186.8, -303.34) * mm});
            skLineSegment(sketch, "E239", {"start": v(171.63, -28) * mm, "end": v(171.63, -18) * mm});
            skLineSegment(sketch, "E240", {"start": v(171.63, -18) * mm, "end": v(175.63, -18) * mm});
            skLineSegment(sketch, "E241", {"start": v(175.63, -18) * mm, "end": v(175.63, -28) * mm});
            skLineSegment(sketch, "E242", {"start": v(175.63, -28) * mm, "end": v(171.63, -28) * mm});
            skLineSegment(sketch, "E243", {"start": v(171.63, -53) * mm, "end": v(171.63, -43) * mm});
            skLineSegment(sketch, "E244", {"start": v(171.63, -43) * mm, "end": v(175.63, -43) * mm});
            skLineSegment(sketch, "E245", {"start": v(175.63, -43) * mm, "end": v(175.63, -53) * mm});
            skLineSegment(sketch, "E246", {"start": v(175.63, -53) * mm, "end": v(171.63, -53) * mm});
            skCircle(sketch, "E247", {"center": v(170.63, -35.5) * mm, "radius": 1.6 * mm});
            skPoint(sketch, "E248.end.orphan", {"position": v(-11.92, 174.3) * mm});
            skPoint(sketch, "E249.end.orphan", {"position": v(92.12, 0.1) * mm});
            skLineSegment(sketch, "E250", {"start": v(86.12, -367.9) * mm, "end": v(97.4, -367.9) * mm});
            skLineSegment(sketch, "E251", {"start": v(86.12, -367.9) * mm, "end": v(86.12, -332.78) * mm});
            skPoint(sketch, "E252.orphan", {"position": v(125.38, -49.9) * mm});
            skLineSegment(sketch, "E253", {"start": v(86.12, -49.9) * mm, "end": v(86.12, 0.1) * mm});
            skPoint(sketch, "E254.end.orphan", {"position": v(96.46, -49.9) * mm});
            skArc(sketch, "E255", {"start": v(114.8, -57.9) * mm, "mid": v(112.46, -52.24) * mm, "end": v(106.8, -49.9) * mm});
            skSolve(sketch);
        }
        {
            var Q0;
            Q0=makeQuery(id+"F4.imprint","IMPRINT",FACE,{"disambiguationData":[TD([[makeQuery(id+"F4.imprint","IMPRINT",EDGE,{"derivedFrom":sQuery(id+"F4.wireOp",EDGE,"E79")}),1.0]])]});
            extrude(context, id + "F5", {"entities" : qUnion([Q0]), "operationType" : NewBodyOperationType.ADD, "oppositeDirection" : true, "depth" : 3 * mm, "offsetDistance" : 25 * mm});
        }
        {
            var Q0;
            Q0=qCreatedBy(makeId("Right.planeOp"),FACE);
            cPlane(context, id + "F6", {"entities" : qUnion([Q0]), "cplaneType" : CPlaneType.OFFSET, "offset" : 118.6 * mm, "width" : 150 * mm, "height" : 150 * mm});
        }
        {
            var Q0;
            Q0=qCreatedBy(id+"F6.planeOp",FACE);
            var sketch = newSketch(context, id + "F7", { "sketchPlane" : qUnion([Q0])});
            skLineSegment(sketch, "E256", {"start": v(-37, -368) * mm, "end": v(-37, -359.47) * mm});
            skArc(sketch, "E257", {"start": v(-36.75, -359.03) * mm, "mid": v(-36.93, -359.22) * mm, "end": v(-37, -359.47) * mm});
            skArc(sketch, "E258", {"start": v(-36.75, -359.03) * mm, "mid": v(-36.65, -358.25) * mm, "end": v(-37.43, -358.35) * mm});
            skArc(sketch, "E259", {"start": v(-37.87, -358.6) * mm, "mid": v(-37.62, -358.53) * mm, "end": v(-37.43, -358.35) * mm});
            skArc(sketch, "E260", {"start": v(-37.43, -331.65) * mm, "mid": v(-37.62, -331.47) * mm, "end": v(-37.87, -331.4) * mm});
            skArc(sketch, "E261", {"start": v(-37.43, -331.65) * mm, "mid": v(-36.65, -331.75) * mm, "end": v(-36.75, -330.97) * mm});
            skArc(sketch, "E262", {"start": v(-37, -330.53) * mm, "mid": v(-36.93, -330.78) * mm, "end": v(-36.75, -330.97) * mm});
            skLineSegment(sketch, "E263", {"start": v(-37, -330.53) * mm, "end": v(-37, -319.47) * mm});
            skArc(sketch, "E264", {"start": v(-36.75, -319.03) * mm, "mid": v(-36.93, -319.22) * mm, "end": v(-37, -319.47) * mm});
            skArc(sketch, "E265", {"start": v(-36.75, -319.03) * mm, "mid": v(-36.65, -318.25) * mm, "end": v(-37.43, -318.35) * mm});
            skArc(sketch, "E266", {"start": v(-37.87, -318.6) * mm, "mid": v(-37.62, -318.53) * mm, "end": v(-37.43, -318.35) * mm});
            skLineSegment(sketch, "E267", {"start": v(-37.87, -318.6) * mm, "end": v(-39.5, -318.6) * mm});
            skArc(sketch, "E268", {"start": v(-40, -318.1) * mm, "mid": v(-39.85, -318.45) * mm, "end": v(-39.5, -318.6) * mm});
            skLineSegment(sketch, "E269", {"start": v(-40, -318.1) * mm, "end": v(-40, -313.1) * mm});
            skArc(sketch, "E270", {"start": v(-39.5, -312.6) * mm, "mid": v(-39.85, -312.75) * mm, "end": v(-40, -313.1) * mm});
            skLineSegment(sketch, "E271", {"start": v(-39.5, -312.6) * mm, "end": v(-37.87, -312.6) * mm});
            skArc(sketch, "E272", {"start": v(-37.43, -312.85) * mm, "mid": v(-37.62, -312.67) * mm, "end": v(-37.87, -312.6) * mm});
            skArc(sketch, "E273", {"start": v(-37.43, -312.85) * mm, "mid": v(-36.65, -312.95) * mm, "end": v(-36.75, -312.17) * mm});
            skArc(sketch, "E274", {"start": v(-37, -311.73) * mm, "mid": v(-36.93, -311.98) * mm, "end": v(-36.75, -312.17) * mm});
            skLineSegment(sketch, "E275", {"start": v(-37, -311.73) * mm, "end": v(-37, -306.6) * mm});
            skLineSegment(sketch, "E276", {"start": v(-37, -306.6) * mm, "end": v(-34, -306.6) * mm});
            skLineSegment(sketch, "E277", {"start": v(-34, -306.6) * mm, "end": v(-34, -307.88) * mm});
            skLineSegment(sketch, "E278", {"start": v(-34, -307.88) * mm, "end": v(-30, -307.88) * mm});
            skLineSegment(sketch, "E279", {"start": v(-30, -307.88) * mm, "end": v(-30, -306.6) * mm});
            skLineSegment(sketch, "E280", {"start": v(-30, -306.6) * mm, "end": v(-27, -306.6) * mm});
            skLineSegment(sketch, "E281", {"start": v(-27, -306.6) * mm, "end": v(-27, -303.4) * mm});
            skLineSegment(sketch, "E282", {"start": v(-27, -303.4) * mm, "end": v(-30, -303.4) * mm});
            skLineSegment(sketch, "E283", {"start": v(-30, -303.4) * mm, "end": v(-30, -302.13) * mm});
            skLineSegment(sketch, "E284", {"start": v(-30, -302.13) * mm, "end": v(-34, -302.13) * mm});
            skLineSegment(sketch, "E285", {"start": v(-34, -302.13) * mm, "end": v(-34, -303.4) * mm});
            skLineSegment(sketch, "E286", {"start": v(-34, -303.4) * mm, "end": v(-37, -303.4) * mm});
            skLineSegment(sketch, "E287", {"start": v(-37, -303.4) * mm, "end": v(-37, -298.27) * mm});
            skArc(sketch, "E288", {"start": v(-36.75, -297.83) * mm, "mid": v(-36.93, -298.02) * mm, "end": v(-37, -298.27) * mm});
            skArc(sketch, "E289", {"start": v(-36.75, -297.83) * mm, "mid": v(-36.65, -297.05) * mm, "end": v(-37.43, -297.15) * mm});
            skArc(sketch, "E290", {"start": v(-37.87, -297.4) * mm, "mid": v(-37.62, -297.33) * mm, "end": v(-37.43, -297.15) * mm});
            skLineSegment(sketch, "E291", {"start": v(-37.87, -297.4) * mm, "end": v(-39.5, -297.4) * mm});
            skArc(sketch, "E292", {"start": v(-40, -296.9) * mm, "mid": v(-39.85, -297.25) * mm, "end": v(-39.5, -297.4) * mm});
            skLineSegment(sketch, "E293", {"start": v(-40, -296.9) * mm, "end": v(-40, -291.9) * mm});
            skArc(sketch, "E294", {"start": v(-39.5, -291.4) * mm, "mid": v(-39.85, -291.55) * mm, "end": v(-40, -291.9) * mm});
            skLineSegment(sketch, "E295", {"start": v(-39.5, -291.4) * mm, "end": v(-37.87, -291.4) * mm});
            skArc(sketch, "E296", {"start": v(-37.43, -291.65) * mm, "mid": v(-37.62, -291.47) * mm, "end": v(-37.87, -291.4) * mm});
            skArc(sketch, "E297", {"start": v(-37.43, -291.65) * mm, "mid": v(-36.65, -291.75) * mm, "end": v(-36.75, -290.97) * mm});
            skArc(sketch, "E298", {"start": v(-37, -290.53) * mm, "mid": v(-36.93, -290.78) * mm, "end": v(-36.75, -290.97) * mm});
            skArc(sketch, "E299", {"start": v(-36.75, -199.03) * mm, "mid": v(-36.93, -199.22) * mm, "end": v(-37, -199.47) * mm});
            skArc(sketch, "E300", {"start": v(-36.75, -199.03) * mm, "mid": v(-36.65, -198.25) * mm, "end": v(-37.43, -198.35) * mm});
            skArc(sketch, "E301", {"start": v(-37.87, -198.6) * mm, "mid": v(-37.62, -198.53) * mm, "end": v(-37.43, -198.35) * mm});
            skLineSegment(sketch, "E302", {"start": v(-37.87, -198.6) * mm, "end": v(-39.5, -198.6) * mm});
            skArc(sketch, "E303", {"start": v(-40, -198.1) * mm, "mid": v(-39.85, -198.45) * mm, "end": v(-39.5, -198.6) * mm});
            skLineSegment(sketch, "E304", {"start": v(-40, -198.1) * mm, "end": v(-40, -193.1) * mm});
            skArc(sketch, "E305", {"start": v(-39.5, -192.6) * mm, "mid": v(-39.85, -192.75) * mm, "end": v(-40, -193.1) * mm});
            skLineSegment(sketch, "E306", {"start": v(-39.5, -192.6) * mm, "end": v(-37.87, -192.6) * mm});
            skArc(sketch, "E307", {"start": v(-37.43, -192.85) * mm, "mid": v(-37.62, -192.67) * mm, "end": v(-37.87, -192.6) * mm});
            skArc(sketch, "E308", {"start": v(-37.43, -192.85) * mm, "mid": v(-36.65, -192.95) * mm, "end": v(-36.75, -192.17) * mm});
            skArc(sketch, "E309", {"start": v(-37, -191.73) * mm, "mid": v(-36.93, -191.98) * mm, "end": v(-36.75, -192.17) * mm});
            skLineSegment(sketch, "E310", {"start": v(-37, -191.73) * mm, "end": v(-37, -186.6) * mm});
            skLineSegment(sketch, "E311", {"start": v(-37, -186.6) * mm, "end": v(-34, -186.6) * mm});
            skLineSegment(sketch, "E312", {"start": v(-34, -186.6) * mm, "end": v(-34, -187.88) * mm});
            skLineSegment(sketch, "E313", {"start": v(-34, -187.88) * mm, "end": v(-30, -187.88) * mm});
            skLineSegment(sketch, "E314", {"start": v(-30, -187.88) * mm, "end": v(-30, -186.6) * mm});
            skLineSegment(sketch, "E315", {"start": v(-30, -186.6) * mm, "end": v(-27, -186.6) * mm});
            skLineSegment(sketch, "E316", {"start": v(-27, -186.6) * mm, "end": v(-27, -183.4) * mm});
            skLineSegment(sketch, "E317", {"start": v(-27, -183.4) * mm, "end": v(-30, -183.4) * mm});
            skLineSegment(sketch, "E318", {"start": v(-30, -183.4) * mm, "end": v(-30, -182.13) * mm});
            skLineSegment(sketch, "E319", {"start": v(-30, -182.13) * mm, "end": v(-34, -182.13) * mm});
            skLineSegment(sketch, "E320", {"start": v(-34, -182.13) * mm, "end": v(-34, -183.4) * mm});
            skLineSegment(sketch, "E321", {"start": v(-34, -183.4) * mm, "end": v(-37, -183.4) * mm});
            skLineSegment(sketch, "E322", {"start": v(-37, -183.4) * mm, "end": v(-37, -178.27) * mm});
            skArc(sketch, "E323", {"start": v(-36.75, -177.83) * mm, "mid": v(-36.93, -178.02) * mm, "end": v(-37, -178.27) * mm});
            skArc(sketch, "E324", {"start": v(-36.75, -177.83) * mm, "mid": v(-36.65, -177.05) * mm, "end": v(-37.43, -177.15) * mm});
            skArc(sketch, "E325", {"start": v(-37.87, -177.4) * mm, "mid": v(-37.62, -177.33) * mm, "end": v(-37.43, -177.15) * mm});
            skLineSegment(sketch, "E326", {"start": v(-37.87, -177.4) * mm, "end": v(-39.5, -177.4) * mm});
            skArc(sketch, "E327", {"start": v(-40, -176.9) * mm, "mid": v(-39.85, -177.25) * mm, "end": v(-39.5, -177.4) * mm});
            skLineSegment(sketch, "E328", {"start": v(-40, -176.9) * mm, "end": v(-40, -171.9) * mm});
            skArc(sketch, "E329", {"start": v(-39.5, -171.4) * mm, "mid": v(-39.85, -171.55) * mm, "end": v(-40, -171.9) * mm});
            skLineSegment(sketch, "E330", {"start": v(-39.5, -171.4) * mm, "end": v(-37.87, -171.4) * mm});
            skArc(sketch, "E331", {"start": v(-37.43, -171.65) * mm, "mid": v(-37.62, -171.47) * mm, "end": v(-37.87, -171.4) * mm});
            skArc(sketch, "E332", {"start": v(-37.43, -171.65) * mm, "mid": v(-36.65, -171.75) * mm, "end": v(-36.75, -170.97) * mm});
            skArc(sketch, "E333", {"start": v(-37, -170.53) * mm, "mid": v(-36.93, -170.78) * mm, "end": v(-36.75, -170.97) * mm});
            skArc(sketch, "E334", {"start": v(-36.75, -39.03) * mm, "mid": v(-36.93, -39.22) * mm, "end": v(-37, -39.47) * mm});
            skArc(sketch, "E335", {"start": v(-36.75, -39.03) * mm, "mid": v(-36.65, -38.25) * mm, "end": v(-37.43, -38.35) * mm});
            skArc(sketch, "E336", {"start": v(-37.87, -38.6) * mm, "mid": v(-37.62, -38.53) * mm, "end": v(-37.43, -38.35) * mm});
            skLineSegment(sketch, "E337", {"start": v(-37.87, -38.6) * mm, "end": v(-39.5, -38.6) * mm});
            skArc(sketch, "E338", {"start": v(-40, -38.1) * mm, "mid": v(-39.85, -38.45) * mm, "end": v(-39.5, -38.6) * mm});
            skLineSegment(sketch, "E339", {"start": v(-40, -38.1) * mm, "end": v(-40, -33.1) * mm});
            skArc(sketch, "E340", {"start": v(-39.5, -32.6) * mm, "mid": v(-39.85, -32.75) * mm, "end": v(-40, -33.1) * mm});
            skLineSegment(sketch, "E341", {"start": v(-39.5, -32.6) * mm, "end": v(-37.87, -32.6) * mm});
            skArc(sketch, "E342", {"start": v(-37.43, -32.85) * mm, "mid": v(-37.62, -32.67) * mm, "end": v(-37.87, -32.6) * mm});
            skArc(sketch, "E343", {"start": v(-37.43, -32.85) * mm, "mid": v(-36.65, -32.95) * mm, "end": v(-36.75, -32.17) * mm});
            skArc(sketch, "E344", {"start": v(-37, -31.73) * mm, "mid": v(-36.93, -31.98) * mm, "end": v(-36.75, -32.17) * mm});
            skLineSegment(sketch, "E345", {"start": v(-37, -31.73) * mm, "end": v(-37, -26.6) * mm});
            skLineSegment(sketch, "E346", {"start": v(-37, -26.6) * mm, "end": v(-34, -26.6) * mm});
            skLineSegment(sketch, "E347", {"start": v(-34, -26.6) * mm, "end": v(-34, -27.88) * mm});
            skLineSegment(sketch, "E348", {"start": v(-34, -27.88) * mm, "end": v(-30, -27.88) * mm});
            skLineSegment(sketch, "E349", {"start": v(-30, -27.88) * mm, "end": v(-30, -26.6) * mm});
            skLineSegment(sketch, "E350", {"start": v(-30, -26.6) * mm, "end": v(-27, -26.6) * mm});
            skLineSegment(sketch, "E351", {"start": v(-27, -26.6) * mm, "end": v(-27, -23.4) * mm});
            skLineSegment(sketch, "E352", {"start": v(-27, -23.4) * mm, "end": v(-30, -23.4) * mm});
            skLineSegment(sketch, "E353", {"start": v(-30, -23.4) * mm, "end": v(-30, -22.13) * mm});
            skLineSegment(sketch, "E354", {"start": v(-30, -22.13) * mm, "end": v(-34, -22.13) * mm});
            skLineSegment(sketch, "E355", {"start": v(-34, -22.13) * mm, "end": v(-34, -23.4) * mm});
            skLineSegment(sketch, "E356", {"start": v(-34, -23.4) * mm, "end": v(-37, -23.4) * mm});
            skLineSegment(sketch, "E357", {"start": v(-37, -23.4) * mm, "end": v(-37, -18.27) * mm});
            skArc(sketch, "E358", {"start": v(-36.75, -17.83) * mm, "mid": v(-36.93, -18.02) * mm, "end": v(-37, -18.27) * mm});
            skArc(sketch, "E359", {"start": v(-36.75, -17.83) * mm, "mid": v(-36.65, -17.05) * mm, "end": v(-37.43, -17.15) * mm});
            skArc(sketch, "E360", {"start": v(-37.87, -17.4) * mm, "mid": v(-37.62, -17.33) * mm, "end": v(-37.43, -17.15) * mm});
            skLineSegment(sketch, "E361", {"start": v(-37.87, -17.4) * mm, "end": v(-39.5, -17.4) * mm});
            skArc(sketch, "E362", {"start": v(-40, -16.9) * mm, "mid": v(-39.85, -17.25) * mm, "end": v(-39.5, -17.4) * mm});
            skLineSegment(sketch, "E363", {"start": v(-40, -16.9) * mm, "end": v(-40, -11.9) * mm});
            skArc(sketch, "E364", {"start": v(-39.5, -11.4) * mm, "mid": v(-39.85, -11.55) * mm, "end": v(-40, -11.9) * mm});
            skLineSegment(sketch, "E365", {"start": v(-39.5, -11.4) * mm, "end": v(-37.87, -11.4) * mm});
            skArc(sketch, "E366", {"start": v(-37.43, -11.65) * mm, "mid": v(-37.62, -11.47) * mm, "end": v(-37.87, -11.4) * mm});
            skArc(sketch, "E367", {"start": v(-37.43, -11.65) * mm, "mid": v(-36.65, -11.75) * mm, "end": v(-36.75, -10.97) * mm});
            skArc(sketch, "E368", {"start": v(-37, -10.53) * mm, "mid": v(-36.93, -10.78) * mm, "end": v(-36.75, -10.97) * mm});
            skLineSegment(sketch, "E369", {"start": v(-37, -10.53) * mm, "end": v(-37, 0) * mm});
            skLineSegment(sketch, "E370", {"start": v(-37, 0) * mm, "end": v(-26.35, 0) * mm});
            skLineSegment(sketch, "E371", {"start": v(-26.35, 0) * mm, "end": v(-26.35, -2.23) * mm});
            skArc(sketch, "E372", {"start": v(-26.6, -2.67) * mm, "mid": v(-26.42, -2.48) * mm, "end": v(-26.35, -2.23) * mm});
            skArc(sketch, "E373", {"start": v(-26.6, -2.67) * mm, "mid": v(-26.7, -3.45) * mm, "end": v(-25.92, -3.35) * mm});
            skArc(sketch, "E374", {"start": v(-25.48, -3.1) * mm, "mid": v(-25.73, -3.17) * mm, "end": v(-25.92, -3.35) * mm});
            skLineSegment(sketch, "E375", {"start": v(-25.48, -3.1) * mm, "end": v(-17.95, -3.1) * mm});
            skLineSegment(sketch, "E376", {"start": v(-17.95, -3.1) * mm, "end": v(-17.95, -6.1) * mm});
            skLineSegment(sketch, "E377", {"start": v(-17.95, -6.1) * mm, "end": v(-19.22, -6.1) * mm});
            skLineSegment(sketch, "E378", {"start": v(-19.22, -6.1) * mm, "end": v(-19.22, -10.1) * mm});
            skLineSegment(sketch, "E379", {"start": v(-19.22, -10.1) * mm, "end": v(-17.95, -10.1) * mm});
            skLineSegment(sketch, "E380", {"start": v(-17.95, -10.1) * mm, "end": v(-17.95, -13.1) * mm});
            skLineSegment(sketch, "E381", {"start": v(-17.95, -13.1) * mm, "end": v(-14.75, -13.1) * mm});
            skLineSegment(sketch, "E382", {"start": v(-14.75, -13.1) * mm, "end": v(-14.75, -10.1) * mm});
            skLineSegment(sketch, "E383", {"start": v(-14.75, -10.1) * mm, "end": v(-13.47, -10.1) * mm});
            skLineSegment(sketch, "E384", {"start": v(-13.47, -10.1) * mm, "end": v(-13.47, -6.1) * mm});
            skLineSegment(sketch, "E385", {"start": v(-13.47, -6.1) * mm, "end": v(-14.75, -6.1) * mm});
            skLineSegment(sketch, "E386", {"start": v(-14.75, -6.1) * mm, "end": v(-14.75, -3.1) * mm});
            skLineSegment(sketch, "E387", {"start": v(-35, -161.5) * mm, "end": v(-35, -158.5) * mm});
            skLineSegment(sketch, "E388", {"start": v(-35, -209.5) * mm, "end": v(-35, -206.5) * mm});
            skLineSegment(sketch, "E389", {"start": v(-35, -285.5) * mm, "end": v(-35, -282.5) * mm});
            skLineSegment(sketch, "E390", {"start": v(-35, -106.5) * mm, "end": v(-35, -103.5) * mm});
            skCircle(sketch, "E391", {"center": v(-30, -160) * mm, "radius": 1.55 * mm});
            skCircle(sketch, "E392", {"center": v(-30, -208) * mm, "radius": 1.55 * mm});
            skCircle(sketch, "E393", {"center": v(-30, -284) * mm, "radius": 1.55 * mm});
            skCircle(sketch, "E394", {"center": v(-30, -105) * mm, "radius": 1.55 * mm});
            skLineSegment(sketch, "E395", {"start": v(-35, -49) * mm, "end": v(-35, -46) * mm});
            skArc(sketch, "E396", {"start": v(-26, -33) * mm, "mid": v(-30, -37) * mm, "end": v(-26, -41) * mm});
            skArc(sketch, "E397", {"start": v(-6, -41) * mm, "mid": v(-2, -37) * mm, "end": v(-6, -33) * mm});
            skLineSegment(sketch, "E398", {"start": v(-26, -41) * mm, "end": v(-6, -41) * mm});
            skLineSegment(sketch, "E399", {"start": v(-6, -33) * mm, "end": v(-26, -33) * mm});
            skCircle(sketch, "E400", {"center": v(26, -312) * mm, "radius": 1.55 * mm});
            skCircle(sketch, "E401", {"center": v(36, -312) * mm, "radius": 1.55 * mm});
            skCircle(sketch, "E402", {"center": v(56, -312) * mm, "radius": 1.55 * mm});
            skCircle(sketch, "E403", {"center": v(66, -312) * mm, "radius": 1.55 * mm});
            skCircle(sketch, "E404", {"center": v(-4, -312) * mm, "radius": 1.55 * mm});
            skCircle(sketch, "E405", {"center": v(6, -312) * mm, "radius": 1.55 * mm});
            skLineSegment(sketch, "E406", {"start": v(-37, -290.53) * mm, "end": v(-37, -286) * mm});
            skLineSegment(sketch, "E407", {"start": v(-36.5, -285.5) * mm, "end": v(-35, -285.5) * mm});
            skLineSegment(sketch, "E408", {"start": v(-37, -286) * mm, "end": v(-36.5, -285.5) * mm});
            skLineSegment(sketch, "E409", {"start": v(-35, -282.5) * mm, "end": v(-36.5, -282.5) * mm});
            skLineSegment(sketch, "E410", {"start": v(-37, -282) * mm, "end": v(-36.5, -282.5) * mm});
            skLineSegment(sketch, "E411", {"start": v(-37, -282) * mm, "end": v(-37, -210) * mm});
            skLineSegment(sketch, "E412", {"start": v(-36.5, -209.5) * mm, "end": v(-35, -209.5) * mm});
            skLineSegment(sketch, "E413", {"start": v(-37, -210) * mm, "end": v(-36.5, -209.5) * mm});
            skLineSegment(sketch, "E414", {"start": v(-37, -206) * mm, "end": v(-37, -199.47) * mm});
            skLineSegment(sketch, "E415", {"start": v(-35, -206.5) * mm, "end": v(-36.5, -206.5) * mm});
            skLineSegment(sketch, "E416", {"start": v(-37, -206) * mm, "end": v(-36.5, -206.5) * mm});
            skLineSegment(sketch, "E417", {"start": v(-37, -170.53) * mm, "end": v(-37, -162) * mm});
            skLineSegment(sketch, "E418", {"start": v(-36.5, -161.5) * mm, "end": v(-35, -161.5) * mm});
            skLineSegment(sketch, "E419", {"start": v(-37, -162) * mm, "end": v(-36.5, -161.5) * mm});
            skLineSegment(sketch, "E420", {"start": v(-35, -158.5) * mm, "end": v(-36.5, -158.5) * mm});
            skLineSegment(sketch, "E421", {"start": v(-37, -158) * mm, "end": v(-36.5, -158.5) * mm});
            skLineSegment(sketch, "E422", {"start": v(-37, -158) * mm, "end": v(-37, -107) * mm});
            skLineSegment(sketch, "E423", {"start": v(-36.5, -106.5) * mm, "end": v(-35, -106.5) * mm});
            skLineSegment(sketch, "E424", {"start": v(-37, -107) * mm, "end": v(-36.5, -106.5) * mm});
            skLineSegment(sketch, "E425", {"start": v(-35, -103.5) * mm, "end": v(-36.5, -103.5) * mm});
            skLineSegment(sketch, "E426", {"start": v(-37, -103) * mm, "end": v(-36.5, -103.5) * mm});
            skLineSegment(sketch, "E427", {"start": v(-37, -103) * mm, "end": v(-37, -49.5) * mm});
            skLineSegment(sketch, "E428", {"start": v(-36.5, -49) * mm, "end": v(-35, -49) * mm});
            skLineSegment(sketch, "E429", {"start": v(-37, -49.5) * mm, "end": v(-36.5, -49) * mm});
            skLineSegment(sketch, "E430", {"start": v(-37, -45.5) * mm, "end": v(-37, -39.47) * mm});
            skLineSegment(sketch, "E431", {"start": v(-35, -46) * mm, "end": v(-36.5, -46) * mm});
            skLineSegment(sketch, "E432", {"start": v(-37, -45.5) * mm, "end": v(-36.5, -46) * mm});
            skArc(sketch, "E433", {"start": v(92.75, -330.97) * mm, "mid": v(92.93, -330.78) * mm, "end": v(93, -330.53) * mm});
            skArc(sketch, "E434", {"start": v(92.75, -330.97) * mm, "mid": v(92.65, -331.75) * mm, "end": v(93.43, -331.65) * mm});
            skArc(sketch, "E435", {"start": v(93.87, -331.4) * mm, "mid": v(93.62, -331.47) * mm, "end": v(93.43, -331.65) * mm});
            skLineSegment(sketch, "E436", {"start": v(93.87, -331.4) * mm, "end": v(95.5, -331.4) * mm});
            skArc(sketch, "E437", {"start": v(96, -331.9) * mm, "mid": v(95.85, -331.55) * mm, "end": v(95.5, -331.4) * mm});
            skLineSegment(sketch, "E438", {"start": v(96, -331.9) * mm, "end": v(96, -336.9) * mm});
            skArc(sketch, "E439", {"start": v(95.5, -337.4) * mm, "mid": v(95.85, -337.25) * mm, "end": v(96, -336.9) * mm});
            skLineSegment(sketch, "E440", {"start": v(95.5, -337.4) * mm, "end": v(93.87, -337.4) * mm});
            skArc(sketch, "E441", {"start": v(93.43, -337.15) * mm, "mid": v(93.62, -337.33) * mm, "end": v(93.87, -337.4) * mm});
            skArc(sketch, "E442", {"start": v(93.43, -337.15) * mm, "mid": v(92.65, -337.05) * mm, "end": v(92.75, -337.83) * mm});
            skArc(sketch, "E443", {"start": v(93, -338.27) * mm, "mid": v(92.93, -338.02) * mm, "end": v(92.75, -337.83) * mm});
            skLineSegment(sketch, "E444", {"start": v(93, -338.27) * mm, "end": v(93, -343.4) * mm});
            skLineSegment(sketch, "E445", {"start": v(93, -343.4) * mm, "end": v(90, -343.4) * mm});
            skLineSegment(sketch, "E446", {"start": v(90, -343.4) * mm, "end": v(90, -342.13) * mm});
            skLineSegment(sketch, "E447", {"start": v(90, -342.13) * mm, "end": v(86, -342.13) * mm});
            skLineSegment(sketch, "E448", {"start": v(86, -342.13) * mm, "end": v(86, -343.4) * mm});
            skLineSegment(sketch, "E449", {"start": v(86, -343.4) * mm, "end": v(83, -343.4) * mm});
            skLineSegment(sketch, "E450", {"start": v(83, -343.4) * mm, "end": v(83, -346.6) * mm});
            skLineSegment(sketch, "E451", {"start": v(83, -346.6) * mm, "end": v(86, -346.6) * mm});
            skLineSegment(sketch, "E452", {"start": v(86, -346.6) * mm, "end": v(86, -347.88) * mm});
            skLineSegment(sketch, "E453", {"start": v(86, -347.88) * mm, "end": v(90, -347.88) * mm});
            skLineSegment(sketch, "E454", {"start": v(90, -347.88) * mm, "end": v(90, -346.6) * mm});
            skLineSegment(sketch, "E455", {"start": v(90, -346.6) * mm, "end": v(93, -346.6) * mm});
            skLineSegment(sketch, "E456", {"start": v(93, -346.6) * mm, "end": v(93, -351.73) * mm});
            skArc(sketch, "E457", {"start": v(92.75, -352.17) * mm, "mid": v(92.93, -351.98) * mm, "end": v(93, -351.73) * mm});
            skArc(sketch, "E458", {"start": v(92.75, -352.17) * mm, "mid": v(92.65, -352.95) * mm, "end": v(93.43, -352.85) * mm});
            skArc(sketch, "E459", {"start": v(93.87, -352.6) * mm, "mid": v(93.62, -352.67) * mm, "end": v(93.43, -352.85) * mm});
            skLineSegment(sketch, "E460", {"start": v(93.87, -352.6) * mm, "end": v(95.5, -352.6) * mm});
            skArc(sketch, "E461", {"start": v(96, -353.1) * mm, "mid": v(95.85, -352.75) * mm, "end": v(95.5, -352.6) * mm});
            skLineSegment(sketch, "E462", {"start": v(96, -353.1) * mm, "end": v(96, -358.1) * mm});
            skArc(sketch, "E463", {"start": v(95.5, -358.6) * mm, "mid": v(95.85, -358.45) * mm, "end": v(96, -358.1) * mm});
            skLineSegment(sketch, "E464", {"start": v(95.5, -358.6) * mm, "end": v(93.87, -358.6) * mm});
            skArc(sketch, "E465", {"start": v(93.43, -358.35) * mm, "mid": v(93.62, -358.53) * mm, "end": v(93.87, -358.6) * mm});
            skArc(sketch, "E466", {"start": v(93.43, -358.35) * mm, "mid": v(92.65, -358.25) * mm, "end": v(92.75, -359.03) * mm});
            skArc(sketch, "E467", {"start": v(93, -359.47) * mm, "mid": v(92.93, -359.22) * mm, "end": v(92.75, -359.03) * mm});
            skLineSegment(sketch, "E468", {"start": v(93, -359.47) * mm, "end": v(93, -370) * mm});
            skLineSegment(sketch, "E469", {"start": v(93, -325.55) * mm, "end": v(93, -330.53) * mm});
            skLineSegment(sketch, "E470", {"start": v(82.35, 0) * mm, "end": v(82.35, -2.23) * mm});
            skArc(sketch, "E471", {"start": v(81.92, -3.35) * mm, "mid": v(82.7, -3.45) * mm, "end": v(82.6, -2.67) * mm});
            skLineSegment(sketch, "E472", {"start": v(93, -370) * mm, "end": v(72.83, -370) * mm});
            skArc(sketch, "E473", {"start": v(71.41, -369.41) * mm, "mid": v(72.06, -369.85) * mm, "end": v(72.83, -370) * mm});
            skLineSegment(sketch, "E474", {"start": v(71.41, -369.41) * mm, "end": v(70.59, -368.59) * mm});
            skArc(sketch, "E475", {"start": v(70.59, -368.59) * mm, "mid": v(69.94, -368.15) * mm, "end": v(69.17, -368) * mm});
            skLineSegment(sketch, "E476", {"start": v(93, 0) * mm, "end": v(82.35, 0) * mm});
            skLineSegment(sketch, "E477", {"start": v(73.95, -6.1) * mm, "end": v(75.23, -6.1) * mm});
            skLineSegment(sketch, "E478", {"start": v(75.23, -6.1) * mm, "end": v(75.23, -10.1) * mm});
            skLineSegment(sketch, "E479", {"start": v(75.23, -10.1) * mm, "end": v(73.95, -10.1) * mm});
            skLineSegment(sketch, "E480", {"start": v(73.95, -10.1) * mm, "end": v(73.95, -13.1) * mm});
            skLineSegment(sketch, "E481", {"start": v(73.95, -13.1) * mm, "end": v(70.75, -13.1) * mm});
            skLineSegment(sketch, "E482", {"start": v(70.75, -13.1) * mm, "end": v(70.75, -10.1) * mm});
            skLineSegment(sketch, "E483", {"start": v(70.75, -10.1) * mm, "end": v(69.48, -10.1) * mm});
            skLineSegment(sketch, "E484", {"start": v(69.48, -10.1) * mm, "end": v(69.48, -6.1) * mm});
            skLineSegment(sketch, "E485", {"start": v(69.48, -6.1) * mm, "end": v(70.75, -6.1) * mm});
            skLineSegment(sketch, "E486", {"start": v(81.48, -3.1) * mm, "end": v(73.95, -3.1) * mm});
            skLineSegment(sketch, "E487", {"start": v(70.75, -6.1) * mm, "end": v(70.75, -3.1) * mm});
            skLineSegment(sketch, "E488", {"start": v(-14.75, -3.1) * mm, "end": v(70.75, -3.1) * mm});
            skLineSegment(sketch, "E489", {"start": v(69.17, -368) * mm, "end": v(-37, -368) * mm});
            skArc(sketch, "E490", {"start": v(53.8, -147) * mm, "mid": v(56, -149.2) * mm, "end": v(58.2, -147) * mm});
            skArc(sketch, "E491", {"start": v(3.8, -147) * mm, "mid": v(6, -149.2) * mm, "end": v(8.2, -147) * mm});
            skArc(sketch, "E492", {"start": v(63, -166) * mm, "mid": v(64.17, -168.83) * mm, "end": v(67, -170) * mm});
            skLineSegment(sketch, "E493", {"start": v(79, -170) * mm, "end": v(67, -170) * mm});
            skArc(sketch, "E494", {"start": v(79, -170) * mm, "mid": v(81.83, -168.83) * mm, "end": v(83, -166) * mm});
            skArc(sketch, "E495", {"start": v(67, -184) * mm, "mid": v(64.17, -185.17) * mm, "end": v(63, -188) * mm});
            skLineSegment(sketch, "E496", {"start": v(79, -184) * mm, "end": v(67, -184) * mm});
            skArc(sketch, "E497", {"start": v(83, -188) * mm, "mid": v(81.83, -185.17) * mm, "end": v(79, -184) * mm});
            skArc(sketch, "E498", {"start": v(-5, -170) * mm, "mid": v(-2.17, -168.83) * mm, "end": v(-1, -166) * mm});
            skLineSegment(sketch, "E499", {"start": v(-17, -170) * mm, "end": v(-5, -170) * mm});
            skArc(sketch, "E500", {"start": v(-21, -166) * mm, "mid": v(-19.83, -168.83) * mm, "end": v(-17, -170) * mm});
            skArc(sketch, "E501", {"start": v(-1, -188) * mm, "mid": v(-2.17, -185.17) * mm, "end": v(-5, -184) * mm});
            skLineSegment(sketch, "E502", {"start": v(-17, -184) * mm, "end": v(-5, -184) * mm});
            skArc(sketch, "E503", {"start": v(-17, -184) * mm, "mid": v(-19.83, -185.17) * mm, "end": v(-21, -188) * mm});
            skArc(sketch, "E504", {"start": v(45, -170) * mm, "mid": v(47.83, -168.83) * mm, "end": v(49, -166) * mm});
            skArc(sketch, "E505", {"start": v(13, -166) * mm, "mid": v(14.17, -168.83) * mm, "end": v(17, -170) * mm});
            skLineSegment(sketch, "E506", {"start": v(17, -170) * mm, "end": v(45, -170) * mm});
            skArc(sketch, "E507", {"start": v(49, -188) * mm, "mid": v(47.83, -185.17) * mm, "end": v(45, -184) * mm});
            skArc(sketch, "E508", {"start": v(17, -184) * mm, "mid": v(14.17, -185.17) * mm, "end": v(13, -188) * mm});
            skLineSegment(sketch, "E509", {"start": v(17, -184) * mm, "end": v(45, -184) * mm});
            skArc(sketch, "E510", {"start": v(-1, -74) * mm, "mid": v(-2.17, -71.17) * mm, "end": v(-5, -70) * mm});
            skLineSegment(sketch, "E511", {"start": v(-5, -70) * mm, "end": v(-17, -70) * mm});
            skArc(sketch, "E512", {"start": v(-17, -70) * mm, "mid": v(-19.83, -71.17) * mm, "end": v(-21, -74) * mm});
            skLineSegment(sketch, "E513", {"start": v(-1, -166) * mm, "end": v(-1, -74) * mm});
            skLineSegment(sketch, "E514", {"start": v(-21, -74) * mm, "end": v(-21, -166) * mm});
            skArc(sketch, "E515", {"start": v(49, -74) * mm, "mid": v(47.83, -71.17) * mm, "end": v(45, -70) * mm});
            skLineSegment(sketch, "E516", {"start": v(49, -166) * mm, "end": v(49, -74) * mm});
            skArc(sketch, "E517", {"start": v(17, -70) * mm, "mid": v(14.17, -71.17) * mm, "end": v(13, -74) * mm});
            skLineSegment(sketch, "E518", {"start": v(13, -166) * mm, "end": v(13, -74) * mm});
            skLineSegment(sketch, "E519", {"start": v(17, -70) * mm, "end": v(45, -70) * mm});
            skArc(sketch, "E520", {"start": v(67, -70) * mm, "mid": v(64.17, -71.17) * mm, "end": v(63, -74) * mm});
            skLineSegment(sketch, "E521", {"start": v(67, -70) * mm, "end": v(79, -70) * mm});
            skArc(sketch, "E522", {"start": v(83, -74) * mm, "mid": v(81.83, -71.17) * mm, "end": v(79, -70) * mm});
            skLineSegment(sketch, "E523", {"start": v(63, -166) * mm, "end": v(63, -74) * mm});
            skLineSegment(sketch, "E524", {"start": v(83, -74) * mm, "end": v(83, -166) * mm});
            skArc(sketch, "E525", {"start": v(-5, -284) * mm, "mid": v(-2.17, -282.83) * mm, "end": v(-1, -280) * mm});
            skLineSegment(sketch, "E526", {"start": v(-5, -284) * mm, "end": v(-17, -284) * mm});
            skArc(sketch, "E527", {"start": v(-21, -280) * mm, "mid": v(-19.83, -282.83) * mm, "end": v(-17, -284) * mm});
            skLineSegment(sketch, "E528", {"start": v(-1, -188) * mm, "end": v(-1, -280) * mm});
            skLineSegment(sketch, "E529", {"start": v(-21, -280) * mm, "end": v(-21, -188) * mm});
            skArc(sketch, "E530", {"start": v(45, -284) * mm, "mid": v(47.83, -282.83) * mm, "end": v(49, -280) * mm});
            skLineSegment(sketch, "E531", {"start": v(49, -188) * mm, "end": v(49, -280) * mm});
            skArc(sketch, "E532", {"start": v(13, -280) * mm, "mid": v(14.17, -282.83) * mm, "end": v(17, -284) * mm});
            skLineSegment(sketch, "E533", {"start": v(13, -188) * mm, "end": v(13, -280) * mm});
            skLineSegment(sketch, "E534", {"start": v(17, -284) * mm, "end": v(45, -284) * mm});
            skArc(sketch, "E535", {"start": v(63, -280) * mm, "mid": v(64.17, -282.83) * mm, "end": v(67, -284) * mm});
            skLineSegment(sketch, "E536", {"start": v(67, -284) * mm, "end": v(79, -284) * mm});
            skArc(sketch, "E537", {"start": v(79, -284) * mm, "mid": v(81.83, -282.83) * mm, "end": v(83, -280) * mm});
            skLineSegment(sketch, "E538", {"start": v(63, -188) * mm, "end": v(63, -280) * mm});
            skLineSegment(sketch, "E539", {"start": v(83, -280) * mm, "end": v(83, -188) * mm});
            skCircle(sketch, "E540", {"center": v(-27, -47) * mm, "radius": 1.55 * mm});
            skCircle(sketch, "E541", {"center": v(-17, -47) * mm, "radius": 1.55 * mm});
            skCircle(sketch, "E542", {"center": v(-4, -47) * mm, "radius": 1.55 * mm});
            skCircle(sketch, "E543", {"center": v(6, -47) * mm, "radius": 1.55 * mm});
            skCircle(sketch, "E544", {"center": v(26, -47) * mm, "radius": 1.55 * mm});
            skCircle(sketch, "E545", {"center": v(36, -47) * mm, "radius": 1.55 * mm});
            skCircle(sketch, "E546", {"center": v(56, -47) * mm, "radius": 1.55 * mm});
            skCircle(sketch, "E547", {"center": v(66, -47) * mm, "radius": 1.55 * mm});
            skCircle(sketch, "E548", {"center": v(78, -47) * mm, "radius": 1.55 * mm});
            skArc(sketch, "E549", {"start": v(8.2, -67) * mm, "mid": v(6, -64.8) * mm, "end": v(3.8, -67) * mm});
            skLineSegment(sketch, "E550", {"start": v(8.2, -67) * mm, "end": v(8.2, -147) * mm});
            skLineSegment(sketch, "E551", {"start": v(3.8, -67) * mm, "end": v(3.8, -147) * mm});
            skArc(sketch, "E552", {"start": v(58.2, -67) * mm, "mid": v(56, -64.8) * mm, "end": v(53.8, -67) * mm});
            skLineSegment(sketch, "E553", {"start": v(58.2, -67) * mm, "end": v(58.2, -147) * mm});
            skLineSegment(sketch, "E554", {"start": v(53.8, -67) * mm, "end": v(53.8, -147) * mm});
            skArc(sketch, "E555", {"start": v(58.2, -207) * mm, "mid": v(56, -204.8) * mm, "end": v(53.8, -207) * mm});
            skArc(sketch, "E556", {"start": v(8.2, -207) * mm, "mid": v(6, -204.8) * mm, "end": v(3.8, -207) * mm});
            skArc(sketch, "E557", {"start": v(3.8, -287) * mm, "mid": v(6, -289.2) * mm, "end": v(8.2, -287) * mm});
            skLineSegment(sketch, "E558", {"start": v(8.2, -287) * mm, "end": v(8.2, -207) * mm});
            skLineSegment(sketch, "E559", {"start": v(3.8, -287) * mm, "end": v(3.8, -207) * mm});
            skArc(sketch, "E560", {"start": v(53.8, -287) * mm, "mid": v(56, -289.2) * mm, "end": v(58.2, -287) * mm});
            skLineSegment(sketch, "E561", {"start": v(58.2, -287) * mm, "end": v(58.2, -207) * mm});
            skLineSegment(sketch, "E562", {"start": v(53.8, -287) * mm, "end": v(53.8, -207) * mm});
            skArc(sketch, "E563", {"start": v(83, -31.5) * mm, "mid": v(81.4, -33.1) * mm, "end": v(83, -34.7) * mm});
            skLineSegment(sketch, "E564", {"start": v(83, -31.5) * mm, "end": v(92.75, -31.5) * mm});
            skLineSegment(sketch, "E565", {"start": v(93, -31.25) * mm, "end": v(93, 0) * mm});
            skLineSegment(sketch, "E566", {"start": v(92.75, -31.5) * mm, "end": v(93, -31.25) * mm});
            skLineSegment(sketch, "E567", {"start": v(83, -34.7) * mm, "end": v(92.75, -34.7) * mm});
            skLineSegment(sketch, "E568", {"start": v(93, -325.55) * mm, "end": v(93, -34.95) * mm});
            skLineSegment(sketch, "E569", {"start": v(92.75, -34.7) * mm, "end": v(93, -34.95) * mm});
            skLineSegment(sketch, "E570", {"start": v(-46.55, -331.4) * mm, "end": v(-46.55, -358.6) * mm});
            skLineSegment(sketch, "E571", {"start": v(-37.87, -331.4) * mm, "end": v(-46.55, -331.4) * mm});
            skLineSegment(sketch, "E572", {"start": v(-37.87, -358.6) * mm, "end": v(-46.55, -358.6) * mm});
            skPoint(sketch, "E573.start.orphan", {"position": v(-40, -174.4) * mm});
            skPoint(sketch, "E574.orphan", {"position": v(77.72, -3.1) * mm});
            skArc(sketch, "E575", {"start": v(81.48, -3.1) * mm, "mid": v(81.73, -3.17) * mm, "end": v(81.92, -3.35) * mm});
            skArc(sketch, "E576", {"start": v(82.6, -2.67) * mm, "mid": v(82.38, -2.41) * mm, "end": v(82.35, -2.08) * mm});
            skLineSegment(sketch, "E577", {"start": v(73.95, -3.1) * mm, "end": v(73.95, -6.1) * mm});
            skSolve(sketch);
        }
        {
            var Q0;
            {var subQ0=sQuery(id+"F7.wireOp",EDGE,"E256");Q0=makeQuery(id+"F7.imprint","IMPRINT",FACE,{"disambiguationData":[TD([[makeQuery(id+"F7.imprint","IMPRINT",EDGE,{"derivedFrom":subQ0}),-1.0]])]});}
            extrude(context, id + "F8", {"entities" : qUnion([Q0]), "depth" : 3 * mm, "offsetDistance" : 25 * mm});
        }
        {
            var Q0;
            Q0=makeQuery(id+"F8.opExtrude","CAP_FACE",FACE,{"disambiguationData":[OSD([sQuery(id+"F7.wireOp",EDGE,"E256"),sQuery(id+"F7.wireOp",EDGE,"E257"),sQuery(id+"F7.wireOp",EDGE,"E258"),sQuery(id+"F7.wireOp",EDGE,"E259"),sQuery(id+"F7.wireOp",EDGE,"E260"),sQuery(id+"F7.wireOp",EDGE,"E261"),sQuery(id+"F7.wireOp",EDGE,"E262"),sQuery(id+"F7.wireOp",EDGE,"E263"),sQuery(id+"F7.wireOp",EDGE,"E264"),sQuery(id+"F7.wireOp",EDGE,"E265"),sQuery(id+"F7.wireOp",EDGE,"E266"),sQuery(id+"F7.wireOp",EDGE,"E267"),sQuery(id+"F7.wireOp",EDGE,"E268"),sQuery(id+"F7.wireOp",EDGE,"E269"),sQuery(id+"F7.wireOp",EDGE,"E270"),sQuery(id+"F7.wireOp",EDGE,"E271"),sQuery(id+"F7.wireOp",EDGE,"E272"),sQuery(id+"F7.wireOp",EDGE,"E273"),sQuery(id+"F7.wireOp",EDGE,"E274"),sQuery(id+"F7.wireOp",EDGE,"E275"),sQuery(id+"F7.wireOp",EDGE,"E276"),sQuery(id+"F7.wireOp",EDGE,"E277"),sQuery(id+"F7.wireOp",EDGE,"E278"),sQuery(id+"F7.wireOp",EDGE,"E279"),sQuery(id+"F7.wireOp",EDGE,"E280"),sQuery(id+"F7.wireOp",EDGE,"E281"),sQuery(id+"F7.wireOp",EDGE,"E282"),sQuery(id+"F7.wireOp",EDGE,"E283"),sQuery(id+"F7.wireOp",EDGE,"E284"),sQuery(id+"F7.wireOp",EDGE,"E285"),sQuery(id+"F7.wireOp",EDGE,"E286"),sQuery(id+"F7.wireOp",EDGE,"E287"),sQuery(id+"F7.wireOp",EDGE,"E288"),sQuery(id+"F7.wireOp",EDGE,"E289"),sQuery(id+"F7.wireOp",EDGE,"E290"),sQuery(id+"F7.wireOp",EDGE,"E291"),sQuery(id+"F7.wireOp",EDGE,"E292"),sQuery(id+"F7.wireOp",EDGE,"E293"),sQuery(id+"F7.wireOp",EDGE,"E294"),sQuery(id+"F7.wireOp",EDGE,"E295"),sQuery(id+"F7.wireOp",EDGE,"E296"),sQuery(id+"F7.wireOp",EDGE,"E297"),sQuery(id+"F7.wireOp",EDGE,"E298"),sQuery(id+"F7.wireOp",EDGE,"E299"),sQuery(id+"F7.wireOp",EDGE,"E300"),sQuery(id+"F7.wireOp",EDGE,"E301"),sQuery(id+"F7.wireOp",EDGE,"E302"),sQuery(id+"F7.wireOp",EDGE,"E303"),sQuery(id+"F7.wireOp",EDGE,"E304"),sQuery(id+"F7.wireOp",EDGE,"E305"),sQuery(id+"F7.wireOp",EDGE,"E306"),sQuery(id+"F7.wireOp",EDGE,"E307"),sQuery(id+"F7.wireOp",EDGE,"E308"),sQuery(id+"F7.wireOp",EDGE,"E309"),sQuery(id+"F7.wireOp",EDGE,"E310"),sQuery(id+"F7.wireOp",EDGE,"E311"),sQuery(id+"F7.wireOp",EDGE,"E312"),sQuery(id+"F7.wireOp",EDGE,"E313"),sQuery(id+"F7.wireOp",EDGE,"E314"),sQuery(id+"F7.wireOp",EDGE,"E315"),sQuery(id+"F7.wireOp",EDGE,"E316"),sQuery(id+"F7.wireOp",EDGE,"E317"),sQuery(id+"F7.wireOp",EDGE,"E318"),sQuery(id+"F7.wireOp",EDGE,"E319"),sQuery(id+"F7.wireOp",EDGE,"E320"),sQuery(id+"F7.wireOp",EDGE,"E321"),sQuery(id+"F7.wireOp",EDGE,"E322"),sQuery(id+"F7.wireOp",EDGE,"E323"),sQuery(id+"F7.wireOp",EDGE,"E324"),sQuery(id+"F7.wireOp",EDGE,"E325"),sQuery(id+"F7.wireOp",EDGE,"E326"),sQuery(id+"F7.wireOp",EDGE,"E327"),sQuery(id+"F7.wireOp",EDGE,"E328"),sQuery(id+"F7.wireOp",EDGE,"E329"),sQuery(id+"F7.wireOp",EDGE,"E330"),sQuery(id+"F7.wireOp",EDGE,"E331"),sQuery(id+"F7.wireOp",EDGE,"E332"),sQuery(id+"F7.wireOp",EDGE,"E333"),sQuery(id+"F7.wireOp",EDGE,"E334"),sQuery(id+"F7.wireOp",EDGE,"E335"),sQuery(id+"F7.wireOp",EDGE,"E336"),sQuery(id+"F7.wireOp",EDGE,"E337"),sQuery(id+"F7.wireOp",EDGE,"E338"),sQuery(id+"F7.wireOp",EDGE,"E339"),sQuery(id+"F7.wireOp",EDGE,"E340"),sQuery(id+"F7.wireOp",EDGE,"E341"),sQuery(id+"F7.wireOp",EDGE,"E342"),sQuery(id+"F7.wireOp",EDGE,"E343"),sQuery(id+"F7.wireOp",EDGE,"E344"),sQuery(id+"F7.wireOp",EDGE,"E345"),sQuery(id+"F7.wireOp",EDGE,"E346"),sQuery(id+"F7.wireOp",EDGE,"E347"),sQuery(id+"F7.wireOp",EDGE,"E348"),sQuery(id+"F7.wireOp",EDGE,"E349"),sQuery(id+"F7.wireOp",EDGE,"E350"),sQuery(id+"F7.wireOp",EDGE,"E351"),sQuery(id+"F7.wireOp",EDGE,"E352"),sQuery(id+"F7.wireOp",EDGE,"E353"),sQuery(id+"F7.wireOp",EDGE,"E354"),sQuery(id+"F7.wireOp",EDGE,"E355"),sQuery(id+"F7.wireOp",EDGE,"E356"),sQuery(id+"F7.wireOp",EDGE,"E357"),sQuery(id+"F7.wireOp",EDGE,"E358"),sQuery(id+"F7.wireOp",EDGE,"E359"),sQuery(id+"F7.wireOp",EDGE,"E360"),sQuery(id+"F7.wireOp",EDGE,"E361"),sQuery(id+"F7.wireOp",EDGE,"E362"),sQuery(id+"F7.wireOp",EDGE,"E363"),sQuery(id+"F7.wireOp",EDGE,"E364"),sQuery(id+"F7.wireOp",EDGE,"E365"),sQuery(id+"F7.wireOp",EDGE,"E366"),sQuery(id+"F7.wireOp",EDGE,"E367"),sQuery(id+"F7.wireOp",EDGE,"E368"),sQuery(id+"F7.wireOp",EDGE,"E369"),sQuery(id+"F7.wireOp",EDGE,"E370"),sQuery(id+"F7.wireOp",EDGE,"E371"),sQuery(id+"F7.wireOp",EDGE,"E372"),sQuery(id+"F7.wireOp",EDGE,"E373"),sQuery(id+"F7.wireOp",EDGE,"E374"),sQuery(id+"F7.wireOp",EDGE,"E375"),sQuery(id+"F7.wireOp",EDGE,"E376"),sQuery(id+"F7.wireOp",EDGE,"E377"),sQuery(id+"F7.wireOp",EDGE,"E378"),sQuery(id+"F7.wireOp",EDGE,"E379"),sQuery(id+"F7.wireOp",EDGE,"E380"),sQuery(id+"F7.wireOp",EDGE,"E381"),sQuery(id+"F7.wireOp",EDGE,"E382"),sQuery(id+"F7.wireOp",EDGE,"E383"),sQuery(id+"F7.wireOp",EDGE,"E384"),sQuery(id+"F7.wireOp",EDGE,"E385"),sQuery(id+"F7.wireOp",EDGE,"E386"),sQuery(id+"F7.wireOp",EDGE,"E387"),sQuery(id+"F7.wireOp",EDGE,"E388"),sQuery(id+"F7.wireOp",EDGE,"E389"),sQuery(id+"F7.wireOp",EDGE,"E390"),sQuery(id+"F7.wireOp",EDGE,"E391"),sQuery(id+"F7.wireOp",EDGE,"E392"),sQuery(id+"F7.wireOp",EDGE,"E393"),sQuery(id+"F7.wireOp",EDGE,"E394"),sQuery(id+"F7.wireOp",EDGE,"E395"),sQuery(id+"F7.wireOp",EDGE,"E396"),sQuery(id+"F7.wireOp",EDGE,"E397"),sQuery(id+"F7.wireOp",EDGE,"E398"),sQuery(id+"F7.wireOp",EDGE,"E399"),sQuery(id+"F7.wireOp",EDGE,"E400"),sQuery(id+"F7.wireOp",EDGE,"E401"),sQuery(id+"F7.wireOp",EDGE,"E402"),sQuery(id+"F7.wireOp",EDGE,"E403"),sQuery(id+"F7.wireOp",EDGE,"E404"),sQuery(id+"F7.wireOp",EDGE,"E405"),sQuery(id+"F7.wireOp",EDGE,"E406"),sQuery(id+"F7.wireOp",EDGE,"E407"),sQuery(id+"F7.wireOp",EDGE,"E408"),sQuery(id+"F7.wireOp",EDGE,"E409"),sQuery(id+"F7.wireOp",EDGE,"E410"),sQuery(id+"F7.wireOp",EDGE,"E411"),sQuery(id+"F7.wireOp",EDGE,"E412"),sQuery(id+"F7.wireOp",EDGE,"E413"),sQuery(id+"F7.wireOp",EDGE,"E414"),sQuery(id+"F7.wireOp",EDGE,"E415"),sQuery(id+"F7.wireOp",EDGE,"E416"),sQuery(id+"F7.wireOp",EDGE,"E417"),sQuery(id+"F7.wireOp",EDGE,"E418"),sQuery(id+"F7.wireOp",EDGE,"E419"),sQuery(id+"F7.wireOp",EDGE,"E420"),sQuery(id+"F7.wireOp",EDGE,"E421"),sQuery(id+"F7.wireOp",EDGE,"E422"),sQuery(id+"F7.wireOp",EDGE,"E423"),sQuery(id+"F7.wireOp",EDGE,"E424"),sQuery(id+"F7.wireOp",EDGE,"E425"),sQuery(id+"F7.wireOp",EDGE,"E426"),sQuery(id+"F7.wireOp",EDGE,"E427"),sQuery(id+"F7.wireOp",EDGE,"E428"),sQuery(id+"F7.wireOp",EDGE,"E429"),sQuery(id+"F7.wireOp",EDGE,"E430"),sQuery(id+"F7.wireOp",EDGE,"E431"),sQuery(id+"F7.wireOp",EDGE,"E432"),sQuery(id+"F7.wireOp",EDGE,"E433"),sQuery(id+"F7.wireOp",EDGE,"E434"),sQuery(id+"F7.wireOp",EDGE,"E435"),sQuery(id+"F7.wireOp",EDGE,"E436"),sQuery(id+"F7.wireOp",EDGE,"E437"),sQuery(id+"F7.wireOp",EDGE,"E438"),sQuery(id+"F7.wireOp",EDGE,"E439"),sQuery(id+"F7.wireOp",EDGE,"E440"),sQuery(id+"F7.wireOp",EDGE,"E441"),sQuery(id+"F7.wireOp",EDGE,"E442"),sQuery(id+"F7.wireOp",EDGE,"E443"),sQuery(id+"F7.wireOp",EDGE,"E444"),sQuery(id+"F7.wireOp",EDGE,"E445"),sQuery(id+"F7.wireOp",EDGE,"E446"),sQuery(id+"F7.wireOp",EDGE,"E447"),sQuery(id+"F7.wireOp",EDGE,"E448"),sQuery(id+"F7.wireOp",EDGE,"E449"),sQuery(id+"F7.wireOp",EDGE,"E450"),sQuery(id+"F7.wireOp",EDGE,"E451"),sQuery(id+"F7.wireOp",EDGE,"E452"),sQuery(id+"F7.wireOp",EDGE,"E453"),sQuery(id+"F7.wireOp",EDGE,"E454"),sQuery(id+"F7.wireOp",EDGE,"E455"),sQuery(id+"F7.wireOp",EDGE,"E456"),sQuery(id+"F7.wireOp",EDGE,"E457"),sQuery(id+"F7.wireOp",EDGE,"E458"),sQuery(id+"F7.wireOp",EDGE,"E459"),sQuery(id+"F7.wireOp",EDGE,"E460"),sQuery(id+"F7.wireOp",EDGE,"E461"),sQuery(id+"F7.wireOp",EDGE,"E462"),sQuery(id+"F7.wireOp",EDGE,"E463"),sQuery(id+"F7.wireOp",EDGE,"E464"),sQuery(id+"F7.wireOp",EDGE,"E465"),sQuery(id+"F7.wireOp",EDGE,"E466"),sQuery(id+"F7.wireOp",EDGE,"E467"),sQuery(id+"F7.wireOp",EDGE,"E468"),sQuery(id+"F7.wireOp",EDGE,"E469"),sQuery(id+"F7.wireOp",EDGE,"E470"),sQuery(id+"F7.wireOp",EDGE,"E471"),sQuery(id+"F7.wireOp",EDGE,"E472"),sQuery(id+"F7.wireOp",EDGE,"E473"),sQuery(id+"F7.wireOp",EDGE,"E474"),sQuery(id+"F7.wireOp",EDGE,"E475"),sQuery(id+"F7.wireOp",EDGE,"E476"),sQuery(id+"F7.wireOp",EDGE,"E477"),sQuery(id+"F7.wireOp",EDGE,"E478"),sQuery(id+"F7.wireOp",EDGE,"E479"),sQuery(id+"F7.wireOp",EDGE,"E480"),sQuery(id+"F7.wireOp",EDGE,"E481"),sQuery(id+"F7.wireOp",EDGE,"E482"),sQuery(id+"F7.wireOp",EDGE,"E483"),sQuery(id+"F7.wireOp",EDGE,"E484"),sQuery(id+"F7.wireOp",EDGE,"E485"),sQuery(id+"F7.wireOp",EDGE,"E486"),sQuery(id+"F7.wireOp",EDGE,"E487"),sQuery(id+"F7.wireOp",EDGE,"E488"),sQuery(id+"F7.wireOp",EDGE,"E489"),sQuery(id+"F7.wireOp",EDGE,"E490"),sQuery(id+"F7.wireOp",EDGE,"E491"),sQuery(id+"F7.wireOp",EDGE,"E492"),sQuery(id+"F7.wireOp",EDGE,"E493"),sQuery(id+"F7.wireOp",EDGE,"E494"),sQuery(id+"F7.wireOp",EDGE,"E495"),sQuery(id+"F7.wireOp",EDGE,"E496"),sQuery(id+"F7.wireOp",EDGE,"E497"),sQuery(id+"F7.wireOp",EDGE,"E498"),sQuery(id+"F7.wireOp",EDGE,"E499"),sQuery(id+"F7.wireOp",EDGE,"E500"),sQuery(id+"F7.wireOp",EDGE,"E501"),sQuery(id+"F7.wireOp",EDGE,"E502"),sQuery(id+"F7.wireOp",EDGE,"E503"),sQuery(id+"F7.wireOp",EDGE,"E504"),sQuery(id+"F7.wireOp",EDGE,"E505"),sQuery(id+"F7.wireOp",EDGE,"E506"),sQuery(id+"F7.wireOp",EDGE,"E507"),sQuery(id+"F7.wireOp",EDGE,"E508"),sQuery(id+"F7.wireOp",EDGE,"E509"),sQuery(id+"F7.wireOp",EDGE,"E510"),sQuery(id+"F7.wireOp",EDGE,"E511"),sQuery(id+"F7.wireOp",EDGE,"E512"),sQuery(id+"F7.wireOp",EDGE,"E513"),sQuery(id+"F7.wireOp",EDGE,"E514"),sQuery(id+"F7.wireOp",EDGE,"E515"),sQuery(id+"F7.wireOp",EDGE,"E516"),sQuery(id+"F7.wireOp",EDGE,"E517"),sQuery(id+"F7.wireOp",EDGE,"E518"),sQuery(id+"F7.wireOp",EDGE,"E519"),sQuery(id+"F7.wireOp",EDGE,"E520"),sQuery(id+"F7.wireOp",EDGE,"E521"),sQuery(id+"F7.wireOp",EDGE,"E522"),sQuery(id+"F7.wireOp",EDGE,"E523"),sQuery(id+"F7.wireOp",EDGE,"E524"),sQuery(id+"F7.wireOp",EDGE,"E525"),sQuery(id+"F7.wireOp",EDGE,"E526"),sQuery(id+"F7.wireOp",EDGE,"E527"),sQuery(id+"F7.wireOp",EDGE,"E528"),sQuery(id+"F7.wireOp",EDGE,"E529"),sQuery(id+"F7.wireOp",EDGE,"E530"),sQuery(id+"F7.wireOp",EDGE,"E531"),sQuery(id+"F7.wireOp",EDGE,"E532"),sQuery(id+"F7.wireOp",EDGE,"E533"),sQuery(id+"F7.wireOp",EDGE,"E534"),sQuery(id+"F7.wireOp",EDGE,"E535"),sQuery(id+"F7.wireOp",EDGE,"E536"),sQuery(id+"F7.wireOp",EDGE,"E537"),sQuery(id+"F7.wireOp",EDGE,"E538"),sQuery(id+"F7.wireOp",EDGE,"E539"),sQuery(id+"F7.wireOp",EDGE,"E540"),sQuery(id+"F7.wireOp",EDGE,"E541"),sQuery(id+"F7.wireOp",EDGE,"E542"),sQuery(id+"F7.wireOp",EDGE,"E543"),sQuery(id+"F7.wireOp",EDGE,"E544"),sQuery(id+"F7.wireOp",EDGE,"E545"),sQuery(id+"F7.wireOp",EDGE,"E546"),sQuery(id+"F7.wireOp",EDGE,"E547"),sQuery(id+"F7.wireOp",EDGE,"E548"),sQuery(id+"F7.wireOp",EDGE,"E549"),sQuery(id+"F7.wireOp",EDGE,"E550"),sQuery(id+"F7.wireOp",EDGE,"E551"),sQuery(id+"F7.wireOp",EDGE,"E552"),sQuery(id+"F7.wireOp",EDGE,"E553"),sQuery(id+"F7.wireOp",EDGE,"E554"),sQuery(id+"F7.wireOp",EDGE,"E555"),sQuery(id+"F7.wireOp",EDGE,"E556"),sQuery(id+"F7.wireOp",EDGE,"E557"),sQuery(id+"F7.wireOp",EDGE,"E558"),sQuery(id+"F7.wireOp",EDGE,"E559"),sQuery(id+"F7.wireOp",EDGE,"E560"),sQuery(id+"F7.wireOp",EDGE,"E561"),sQuery(id+"F7.wireOp",EDGE,"E562"),sQuery(id+"F7.wireOp",EDGE,"E563"),sQuery(id+"F7.wireOp",EDGE,"E564"),sQuery(id+"F7.wireOp",EDGE,"E565"),sQuery(id+"F7.wireOp",EDGE,"E566"),sQuery(id+"F7.wireOp",EDGE,"E567"),sQuery(id+"F7.wireOp",EDGE,"E568"),sQuery(id+"F7.wireOp",EDGE,"E569"),sQuery(id+"F7.wireOp",EDGE,"E570"),sQuery(id+"F7.wireOp",EDGE,"E571"),sQuery(id+"F7.wireOp",EDGE,"E572"),sQuery(id+"F7.wireOp",EDGE,"E575"),sQuery(id+"F7.wireOp",EDGE,"E576"),sQuery(id+"F7.wireOp",EDGE,"E577")])],"isStart":false});
            var sketch = newSketch(context, id + "F9", { "sketchPlane" : qUnion([Q0])});
            skLineSegment(sketch, "E578.bottom", {"start": v(-27, -73.1) * mm, "end": v(93, -73.1) * mm});
            skLineSegment(sketch, "E578.top", {"start": v(-27, -273.1) * mm, "end": v(93, -273.1) * mm});
            skLineSegment(sketch, "E578.left", {"start": v(-27, -73.1) * mm, "end": v(-27, -273.1) * mm});
            skLineSegment(sketch, "E578.right", {"start": v(93, -73.1) * mm, "end": v(93, -273.1) * mm});
            skLineSegment(sketch, "E579.0", {"start": v(-14.75, -3.1) * mm, "end": v(70.75, -3.1) * mm});
            skLineSegment(sketch, "E580.0", {"start": v(-37, -22.39) * mm, "end": v(-37, -303.34) * mm});
            skSolve(sketch);
        }
        {
            var Q0;
            Q0 = qSketchRegion(id + "F9", true);
            extrude(context, id + "F10", {"entities" : qUnion([Q0]), "flatOperationType" : FlatOperationType.REMOVE, "depth" : (getVariable(context, 'profondeur_alim')) * mm, "offsetDistance" : 25 * mm, "domain" : OperationDomain.MODEL});
        }
    });
